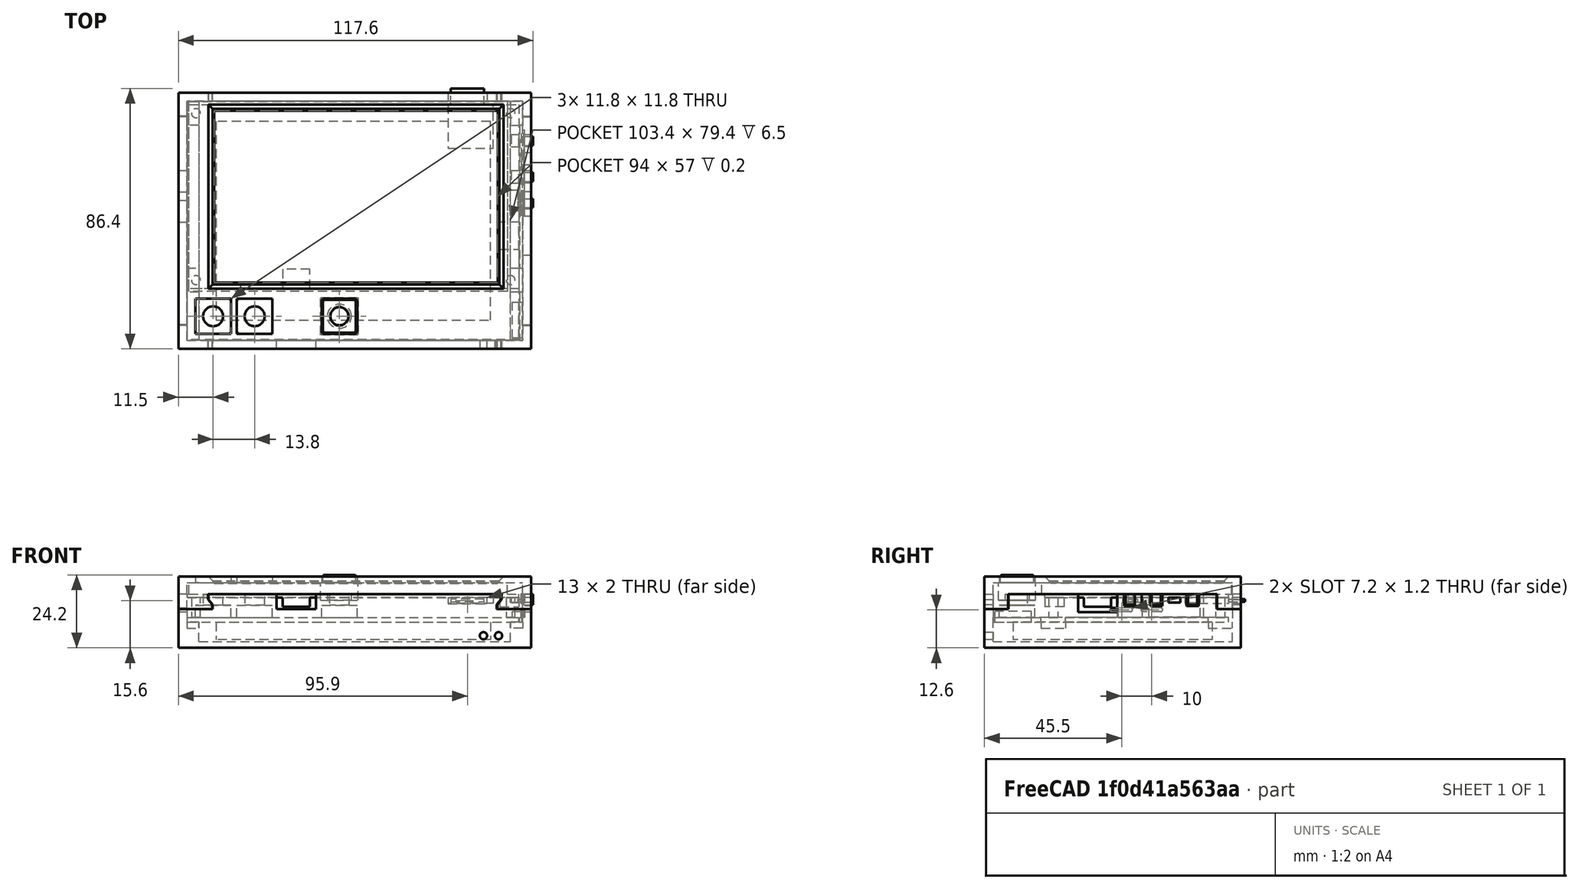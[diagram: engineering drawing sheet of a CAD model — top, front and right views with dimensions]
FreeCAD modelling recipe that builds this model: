
FCSTD DOCUMENT  (FreeCAD 0.19R24276 (Git))
Label: Case-M2
License: All rights reserved
LicenseURL: http://en.wikipedia.org/wiki/All_rights_reserved
objects: Sketcher::SketchObject×50, PartDesign::Pad×27, PartDesign::Pocket×20, PartDesign::ShapeBinder×11, PartDesign::Body×8, Mesh::Feature×3, PartDesign::Chamfer×2, PartDesign::Fillet×1
note: 169 computed .brp shape members not serialized (recipe doc carries the construction recipe); baked Part::Feature solids carry a one-line shape summary decoded from their .brp

FEATURE [Sketcher::SketchObject] Sketch  label="PCB-OUTLINE"
  FullyConstrained = true
  MapMode = 5
  Support = -> [XY_Plane]
  sketch-geometry (41):
    g0: LineSegment StartX=-55 StartY=30.5 StartZ=0 EndX=55 EndY=30.5 EndZ=0
    g1: LineSegment StartX=55 StartY=30.5 StartZ=0 EndX=55 EndY=-30.5 EndZ=0
    g2: LineSegment StartX=55 StartY=-30.5 StartZ=0 EndX=-55 EndY=-30.5 EndZ=0
    g3: LineSegment StartX=-55 StartY=-30.5 StartZ=0 EndX=-55 EndY=30.5 EndZ=0
    g4: Circle CenterX=-52.2 CenterY=27.7 CenterZ=0 NormalX=0 NormalY=0 NormalZ=1 AngleXU=0 Radius=1.6
    g5: Circle CenterX=52.2 CenterY=27.7 CenterZ=0 NormalX=0 NormalY=0 NormalZ=1 AngleXU=0 Radius=1.6
    g6: Circle CenterX=-52.2 CenterY=-27.7 CenterZ=0 NormalX=0 NormalY=0 NormalZ=1 AngleXU=0 Radius=1.6
    g7: Circle CenterX=52.2 CenterY=-27.7 CenterZ=0 NormalX=0 NormalY=0 NormalZ=1 AngleXU=0 Radius=1.6
    g8: LineSegment StartX=31.4 StartY=30.5 StartZ=0 EndX=46.4 EndY=30.5 EndZ=0
    g9: LineSegment StartX=46.4 StartY=30.5 StartZ=0 EndX=46.4 EndY=16 EndZ=0
    g10: LineSegment StartX=46.4 StartY=16 StartZ=0 EndX=31.4 EndY=16 EndZ=0
    g11: LineSegment StartX=31.4 StartY=16 StartZ=0 EndX=31.4 EndY=30.5 EndZ=0
    g12: LineSegment StartX=-23.4 StartY=-24.1 StartZ=0 EndX=-14.4 EndY=-24.1 EndZ=0
    g13: LineSegment StartX=-14.4 StartY=-24.1 StartZ=0 EndX=-14.4 EndY=-30.5 EndZ=0
    g14: LineSegment StartX=-14.4 StartY=-30.5 StartZ=0 EndX=-23.4 EndY=-30.5 EndZ=0
    g15: LineSegment StartX=-23.4 StartY=-30.5 StartZ=0 EndX=-23.4 EndY=-24.1 EndZ=0
    g16: LineSegment StartX=48.6 StartY=-8.5 StartZ=0 EndX=55 EndY=-8.5 EndZ=0
    g17: LineSegment StartX=55 StartY=-8.5 StartZ=0 EndX=55 EndY=-17.5 EndZ=0
    g18: LineSegment StartX=55 StartY=-17.5 StartZ=0 EndX=48.6 EndY=-17.5 EndZ=0
    g19: LineSegment StartX=48.6 StartY=-17.5 StartZ=0 EndX=48.6 EndY=-8.5 EndZ=0
    g20: LineSegment StartX=52 StartY=2.1 StartZ=0 EndX=54.7 EndY=2.1 EndZ=0
    g21: LineSegment StartX=54.7 StartY=2.1 StartZ=0 EndX=54.7 EndY=-4.7 EndZ=0
    g22: LineSegment StartX=54.7 StartY=-4.7 StartZ=0 EndX=52 EndY=-4.7 EndZ=0
    g23: LineSegment StartX=52 StartY=-4.7 StartZ=0 EndX=52 EndY=2.1 EndZ=0
    g24: LineSegment StartX=52.4 StartY=8.5 StartZ=0 EndX=55 EndY=8.5 EndZ=0
    g25: LineSegment StartX=55 StartY=8.5 StartZ=0 EndX=55 EndY=4.5 EndZ=0
    g26: LineSegment StartX=55 StartY=4.5 StartZ=0 EndX=52.4 EndY=4.5 EndZ=0
    g27: LineSegment StartX=52.4 StartY=4.5 StartZ=0 EndX=52.4 EndY=8.5 EndZ=0
    g28: LineSegment StartX=52.4 StartY=20.5 StartZ=0 EndX=55 EndY=20.5 EndZ=0
    g29: LineSegment StartX=55 StartY=20.5 StartZ=0 EndX=55 EndY=16.5 EndZ=0
    g30: LineSegment StartX=55 StartY=16.5 StartZ=0 EndX=52.4 EndY=16.5 EndZ=0
    g31: LineSegment StartX=52.4 StartY=16.5 StartZ=0 EndX=52.4 EndY=20.5 EndZ=0
    g32: LineSegment StartX=32.4 StartY=30.5 StartZ=0 EndX=43.4 EndY=30.5 EndZ=0
    g33: LineSegment StartX=43.4 StartY=30.5 StartZ=0 EndX=43.4 EndY=20.5 EndZ=0
    g34: LineSegment StartX=43.4 StartY=20.5 StartZ=0 EndX=32.4 EndY=20.5 EndZ=0
    g35: LineSegment StartX=32.4 StartY=20.5 StartZ=0 EndX=32.4 EndY=30.5 EndZ=0
    g36: LineSegment StartX=54.7 StartY=0.2 StartZ=0 EndX=56.2 EndY=0.2 EndZ=0
    g37: LineSegment StartX=56.2 StartY=0.2 StartZ=0 EndX=56.2 EndY=-2.8 EndZ=0
    g38: LineSegment StartX=56.2 StartY=-2.8 StartZ=0 EndX=54.7 EndY=-2.8 EndZ=0
    g39: LineSegment StartX=54.7 StartY=-2.8 StartZ=0 EndX=54.7 EndY=0.2 EndZ=0
    g40: LineSegment StartX=54.7 StartY=-1.5 StartZ=0 EndX=56.2 EndY=-1.5 EndZ=0
  constraints (120):
    c: Coincident(g0,g1)
    c: Coincident(g1,g2)
    c: Coincident(g2,g3)
    c: Coincident(g3,g0)
    c: Horizontal(g0)
    c: Vertical(g1)
    c: DistanceX(g2,g2) = 110
    c: Symmetric(g2,g1,g-2)
    c: DistanceY(g3,g3) = 61
    c: Symmetric(g0,g2,g-1)
    c: Symmetric(g6,g7,g-2)
    c: DistanceX(g6,g7) = 104.4
    c: Vertical(g5,g7)
    c: Symmetric(g4,g6,g-1)
    c: Horizontal(g4,g5)
    c: DistanceY(g6,g4) = 55.4
    c: Equal(g4,g6)
    c: Equal(g6,g7)
    c: Equal(g7,g5)
    c: Radius(g4) = 1.6
    c: Coincident(g8,g9)
    c: Coincident(g9,g10)
    c: Coincident(g10,g11)
    c: Coincident(g11,g8)
    c: Horizontal(g8)
    c: Horizontal(g10)
    c: Vertical(g9)
    c: Vertical(g11)
    c: Coincident(g12,g13)
    c: Coincident(g13,g14)
    c: Coincident(g14,g15)
    c: Coincident(g15,g12)
    c: Horizontal(g12)
    c: Horizontal(g14)
    c: Vertical(g13)
    c: Vertical(g15)
    c: Coincident(g16,g17)
    c: Coincident(g17,g18)
    c: Coincident(g18,g19)
    c: Coincident(g19,g16)
    c: Horizontal(g16)
    c: Horizontal(g18)
    c: Vertical(g17)
    c: Vertical(g19)
    c: Coincident(g20,g21)
    c: Coincident(g21,g22)
    c: Coincident(g22,g23)
    c: Coincident(g23,g20)
    c: Horizontal(g20)
    c: Horizontal(g22)
    c: Vertical(g21)
    c: Vertical(g23)
    c: Coincident(g24,g25)
    c: Coincident(g25,g26)
    c: Coincident(g26,g27)
    c: Coincident(g27,g24)
    c: Horizontal(g24)
    c: Horizontal(g26)
    c: Vertical(g25)
    c: Vertical(g27)
    c: Coincident(g28,g29)
    c: Coincident(g29,g30)
    c: Coincident(g30,g31)
    c: Coincident(g31,g28)
    c: Horizontal(g28)
    c: Horizontal(g30)
    c: Vertical(g29)
    c: Vertical(g31)
    c: Equal(g14,g17)
    c: Equal(g18,g13)
    c: DistanceY(g15,g15) = 6.4
    c: DistanceX(g12,g12) = 9
    c: DistanceX(g2,g14) = 31.6
    c: PointOnObject(g14,g2)
    c: PointOnObject(g17,g1)
    c: DistanceY(g1,g17) = 13
    c: DistanceX(g8,g8) = 15
    c: DistanceY(g11,g11) = 14.5
    c: PointOnObject(g8,g0)
    c: Coincident(g32,g33)
    c: Coincident(g33,g34)
    c: Coincident(g34,g35)
    c: Coincident(g35,g32)
    c: Horizontal(g32)
    c: Horizontal(g34)
    c: Vertical(g33)
    c: Vertical(g35)
    c: PointOnObject(g32,g0)
    c: DistanceX(g32,g32) = 11
    c: DistanceX(g8,g32) = 1
    c: DistanceY(g35,g35) = 10
    c: DistanceX(g8,g0) = 8.6
    c: DistanceY(g23,g23) = 6.8
    c: DistanceX(g22,g1) = 3
    c: DistanceX(g22,g22) = 2.7
    c: DistanceY(g20,g0) = 28.4
    c: Equal(g24,g30)
    c: Equal(g27,g31)
    c: PointOnObject(g28,g1)
    c: PointOnObject(g24,g1)
    c: DistanceY(g27,g27) = 4
    c: DistanceX(g26,g26) = 2.6
    c: DistanceY(g24,g0) = 22
    c: DistanceY(g28,g0) = 10
    c: Coincident(g36,g37)
    c: Coincident(g37,g38)
    c: Coincident(g38,g39)
    c: Coincident(g39,g36)
    c: Horizontal(g36)
    c: Horizontal(g38)
    c: Vertical(g37)
    c: Vertical(g39)
    c: PointOnObject(g36,g21)
    c: DistanceY(g37,g37) = 3
    c: DistanceX(g38,g38) = 1.5
    c: DistanceY(g21,g37) = 1.9
    c: PointOnObject(g40,g21)
    c: PointOnObject(g40,g37)
    c: Horizontal(g40)
    c: DistanceY(g37,g40) = 1.3
FEATURE [PartDesign::ShapeBinder] ShapeBinder
  Support = -> [Sketch]
  TraceSupport = false
FEATURE [PartDesign::ShapeBinder] ShapeBinder001
  Support = -> [Sketch]
  TraceSupport = false
FEATURE [Sketcher::SketchObject] Sketch001
  ExternalGeometry = -> [ShapeBinder]
  FullyConstrained = true
  MapMode = 5
  Support = -> [XY_Plane001]
  sketch-geometry (4):
    g0: LineSegment StartX=-55 StartY=30.5 StartZ=0 EndX=55 EndY=30.5 EndZ=0
    g1: LineSegment StartX=55 StartY=30.5 StartZ=0 EndX=55 EndY=-47.5 EndZ=0
    g2: LineSegment StartX=55 StartY=-47.5 StartZ=0 EndX=-55 EndY=-47.5 EndZ=0
    g3: LineSegment StartX=-55 StartY=-47.5 StartZ=0 EndX=-55 EndY=30.5 EndZ=0
  constraints (11):
    c: Coincident(g0,g1)
    c: Coincident(g1,g2)
    c: Coincident(g2,g3)
    c: Coincident(g3,g0)
    c: Horizontal(g0)
    c: Horizontal(g2)
    c: Vertical(g1)
    c: Vertical(g3)
    c: Coincident(g0,g-3)
    c: Vertical(g-4,g1)
    c: DistanceY(g1,g-4) = 17
FEATURE [PartDesign::Pad] Pad
  Direction = (1,1,1)
  Length = 1.6
  Length2 = 100
  Profile = -> Sketch001
  Type = 0
FEATURE [Sketcher::SketchObject] Sketch008  label="LCD_OUTLINE"
  ExternalGeometry = -> [Sketch]
  FullyConstrained = true
  MapMode = 5
  Support = -> [XY_Plane]
  sketch-geometry (8):
    g0: LineSegment StartX=-54.5 StartY=31.5 StartZ=0 EndX=51.1 EndY=31.5 EndZ=0
    g1: LineSegment StartX=51.1 StartY=31.5 StartZ=0 EndX=51.1 EndY=-31.5 EndZ=0
    g2: LineSegment StartX=51.1 StartY=-31.5 StartZ=0 EndX=-54.5 EndY=-31.5 EndZ=0
    g3: LineSegment StartX=-54.5 StartY=-31.5 StartZ=0 EndX=-54.5 EndY=31.5 EndZ=0
    g4: LineSegment StartX=-46.1 StartY=28.5 StartZ=0 EndX=47.9 EndY=28.5 EndZ=0
    g5: LineSegment StartX=47.9 StartY=28.5 StartZ=0 EndX=47.9 EndY=-28.5 EndZ=0
    g6: LineSegment StartX=47.9 StartY=-28.5 StartZ=0 EndX=-46.1 EndY=-28.5 EndZ=0
    g7: LineSegment StartX=-46.1 StartY=-28.5 StartZ=0 EndX=-46.1 EndY=28.5 EndZ=0
  constraints (23):
    c: Coincident(g0,g1)
    c: Coincident(g1,g2)
    c: Coincident(g2,g3)
    c: Coincident(g3,g0)
    c: Horizontal(g0)
    c: Horizontal(g2)
    c: Vertical(g3)
    c: DistanceY(g1,g1) = 63
    c: Symmetric(g1,g0,g-1)
    c: DistanceX(g0,g0) = 105.6
    c: DistanceX(g-3,g0) = 0.5
    c: Coincident(g4,g5)
    c: Coincident(g5,g6)
    c: Coincident(g6,g7)
    c: Coincident(g7,g4)
    c: Horizontal(g4)
    c: Horizontal(g6)
    c: Vertical(g5)
    c: Vertical(g7)
    c: DistanceX(g5,g1) = 3.2
    c: DistanceX(g2,g6) = 8.4
    c: DistanceY(g4,g0) = 3
    c: DistanceY(g1,g5) = 3
FEATURE [PartDesign::ShapeBinder] ShapeBinder002
  Support = -> [Sketch]
  TraceSupport = false
FEATURE [PartDesign::ShapeBinder] ShapeBinder003
  Support = -> [Sketch008]
  TraceSupport = false
FEATURE [Sketcher::SketchObject] Sketch009
  ExternalGeometry = -> [ShapeBinder002]
  FullyConstrained = true
  MapMode = 5
  Placement = pos=(0,0,1.6) rot=(0,0,1;0rad)
  Support = -> [Pad]
  sketch-geometry (4):
    g0: Circle CenterX=-52.2 CenterY=27.7 CenterZ=0 NormalX=0 NormalY=0 NormalZ=1 AngleXU=0 Radius=1.5
    g1: Circle CenterX=-52.2 CenterY=-27.7 CenterZ=0 NormalX=0 NormalY=0 NormalZ=1 AngleXU=0 Radius=1.5
    g2: Circle CenterX=52.2 CenterY=-27.7 CenterZ=0 NormalX=0 NormalY=0 NormalZ=1 AngleXU=0 Radius=1.5
    g3: Circle CenterX=52.2 CenterY=27.7 CenterZ=0 NormalX=0 NormalY=0 NormalZ=1 AngleXU=0 Radius=1.5
  constraints (8):
    c: Coincident(g0,g-3)
    c: Coincident(g1,g-4)
    c: Coincident(g2,g-5)
    c: Coincident(g3,g-6)
    c: Equal(g0,g1)
    c: Equal(g1,g2)
    c: Equal(g2,g3)
    c: Radius(g0) = 1.5
FEATURE [PartDesign::Pad] Pad001
  BaseFeature = -> Pad
  Direction = (1,1,1)
  Length = 6.5
  Length2 = 100
  Profile = -> Sketch009
  Type = 0
FEATURE [Sketcher::SketchObject] Sketch010
  ExternalGeometry = -> [ShapeBinder002]
  FullyConstrained = true
  MapMode = 5
  Placement = pos=(0,0,8.1) rot=(0,0,1;0rad)
  Support = -> [Pad001]
  sketch-geometry (4):
    g0: LineSegment StartX=-55 StartY=30.5 StartZ=0 EndX=55 EndY=30.5 EndZ=0
    g1: LineSegment StartX=55 StartY=30.5 StartZ=0 EndX=55 EndY=-30.5 EndZ=0
    g2: LineSegment StartX=55 StartY=-30.5 StartZ=0 EndX=-55 EndY=-30.5 EndZ=0
    g3: LineSegment StartX=-55 StartY=-30.5 StartZ=0 EndX=-55 EndY=30.5 EndZ=0
  constraints (10):
    c: Coincident(g0,g1)
    c: Coincident(g1,g2)
    c: Coincident(g2,g3)
    c: Coincident(g3,g0)
    c: Horizontal(g0)
    c: Horizontal(g2)
    c: Vertical(g1)
    c: Vertical(g3)
    c: Coincident(g0,g-3)
    c: Coincident(g1,g-4)
FEATURE [PartDesign::Pad] Pad002
  BaseFeature = -> Pad001
  Direction = (1,1,1)
  Length = 1.2
  Length2 = 100
  Profile = -> Sketch010
  Type = 0
FEATURE [Sketcher::SketchObject] Sketch011
  ExternalGeometry = -> [ShapeBinder003]
  FullyConstrained = true
  MapMode = 5
  Placement = pos=(0,0,9.3) rot=(0,0,1;0rad)
  Support = -> [Pad002]
  sketch-geometry (4):
    g0: LineSegment StartX=-54.5 StartY=31.5 StartZ=0 EndX=51.1 EndY=31.5 EndZ=0
    g1: LineSegment StartX=51.1 StartY=31.5 StartZ=0 EndX=51.1 EndY=-31.5 EndZ=0
    g2: LineSegment StartX=51.1 StartY=-31.5 StartZ=0 EndX=-54.5 EndY=-31.5 EndZ=0
    g3: LineSegment StartX=-54.5 StartY=-31.5 StartZ=0 EndX=-54.5 EndY=31.5 EndZ=0
  constraints (10):
    c: Coincident(g0,g1)
    c: Coincident(g1,g2)
    c: Coincident(g2,g3)
    c: Coincident(g3,g0)
    c: Horizontal(g0)
    c: Horizontal(g2)
    c: Vertical(g1)
    c: Vertical(g3)
    c: Coincident(g0,g-3)
    c: Coincident(g1,g-4)
FEATURE [PartDesign::Pad] Pad003
  BaseFeature = -> Pad002
  Direction = (1,1,1)
  Length = 3.8
  Length2 = 100
  Profile = -> Sketch011
  Type = 0
FEATURE [Sketcher::SketchObject] Sketch012
  ExternalGeometry = -> [ShapeBinder003]
  FullyConstrained = true
  MapMode = 5
  Placement = pos=(0,0,13.1) rot=(0,0,1;0rad)
  Support = -> [Pad003]
  sketch-geometry (4):
    g0: LineSegment StartX=-46.1 StartY=28.5 StartZ=0 EndX=47.9 EndY=28.5 EndZ=0
    g1: LineSegment StartX=47.9 StartY=28.5 StartZ=0 EndX=47.9 EndY=-28.5 EndZ=0
    g2: LineSegment StartX=47.9 StartY=-28.5 StartZ=0 EndX=-46.1 EndY=-28.5 EndZ=0
    g3: LineSegment StartX=-46.1 StartY=-28.5 StartZ=0 EndX=-46.1 EndY=28.5 EndZ=0
  constraints (10):
    c: Coincident(g0,g1)
    c: Coincident(g1,g2)
    c: Coincident(g2,g3)
    c: Coincident(g3,g0)
    c: Horizontal(g0)
    c: Horizontal(g2)
    c: Vertical(g1)
    c: Vertical(g3)
    c: Coincident(g0,g-3)
    c: Coincident(g1,g-4)
FEATURE [PartDesign::Pocket] Pocket
  BaseFeature = -> Pad003
  Length = 0.2
  Length2 = 100
  Profile = -> Sketch012
  Type = 0
FEATURE [Sketcher::SketchObject] Sketch013
  ExternalGeometry = -> [ShapeBinder002]
  FullyConstrained = true
  MapMode = 5
  Placement = pos=(0,0,8.1) rot=(1,0,0;3.14159rad)
  Support = -> [Pocket]
  sketch-geometry (8):
    g0: LineSegment StartX=-23.4 StartY=30.5 StartZ=0 EndX=-14.4 EndY=30.5 EndZ=0
    g1: LineSegment StartX=-14.4 StartY=30.5 StartZ=0 EndX=-14.4 EndY=24.1 EndZ=0
    g2: LineSegment StartX=-14.4 StartY=24.1 StartZ=0 EndX=-23.4 EndY=24.1 EndZ=0
    g3: LineSegment StartX=-23.4 StartY=24.1 StartZ=0 EndX=-23.4 EndY=30.5 EndZ=0
    g4: LineSegment StartX=48.6 StartY=17.5 StartZ=0 EndX=55 EndY=17.5 EndZ=0
    g5: LineSegment StartX=55 StartY=17.5 StartZ=0 EndX=55 EndY=8.5 EndZ=0
    g6: LineSegment StartX=55 StartY=8.5 StartZ=0 EndX=48.6 EndY=8.5 EndZ=0
    g7: LineSegment StartX=48.6 StartY=8.5 StartZ=0 EndX=48.6 EndY=17.5 EndZ=0
  constraints (20):
    c: Coincident(g0,g1)
    c: Coincident(g1,g2)
    c: Coincident(g2,g3)
    c: Coincident(g3,g0)
    c: Horizontal(g0)
    c: Horizontal(g2)
    c: Vertical(g1)
    c: Vertical(g3)
    c: Coincident(g0,g-3)
    c: Coincident(g1,g-4)
    c: Coincident(g4,g5)
    c: Coincident(g5,g6)
    c: Coincident(g6,g7)
    c: Coincident(g7,g4)
    c: Horizontal(g4)
    c: Horizontal(g6)
    c: Vertical(g5)
    c: Vertical(g7)
    c: Coincident(g4,g-6)
    c: Coincident(g5,g-5)
FEATURE [PartDesign::Pad] Pad004
  BaseFeature = -> Pocket
  Direction = (1,1,1)
  Length = 3
  Length2 = 100
  Profile = -> Sketch013
  Type = 0
FEATURE [Sketcher::SketchObject] Sketch014
  ExternalGeometry = -> [ShapeBinder002]
  FullyConstrained = true
  MapMode = 5
  Placement = pos=(0,0,8.1) rot=(1,0,0;3.14159rad)
  Support = -> [Pad004]
  sketch-geometry (4):
    g0: LineSegment StartX=31.4 StartY=-16 StartZ=0 EndX=46.4 EndY=-16 EndZ=0
    g1: LineSegment StartX=46.4 StartY=-16 StartZ=0 EndX=46.4 EndY=-30.5 EndZ=0
    g2: LineSegment StartX=46.4 StartY=-30.5 StartZ=0 EndX=31.4 EndY=-30.5 EndZ=0
    g3: LineSegment StartX=31.4 StartY=-30.5 StartZ=0 EndX=31.4 EndY=-16 EndZ=0
  constraints (10):
    c: Coincident(g0,g1)
    c: Coincident(g1,g2)
    c: Coincident(g2,g3)
    c: Coincident(g3,g0)
    c: Horizontal(g0)
    c: Horizontal(g2)
    c: Vertical(g1)
    c: Vertical(g3)
    c: Coincident(g0,g-3)
    c: Coincident(g1,g-4)
FEATURE [PartDesign::Pad] Pad005
  BaseFeature = -> Pad004
  Direction = (1,1,1)
  Length = 1.8
  Length2 = 100
  Profile = -> Sketch014
  Type = 0
FEATURE [Sketcher::SketchObject] Sketch015
  ExternalGeometry = -> [Pad005,ShapeBinder002]
  FullyConstrained = true
  MapMode = 5
  Placement = pos=(0,30.5,0) rot=(0,0.707107,0.707107;3.14159rad)
  Support = -> [Pad005]
  sketch-geometry (4):
    g0: LineSegment StartX=-43.4 StartY=7.6 StartZ=0 EndX=-32.4 EndY=7.6 EndZ=0
    g1: LineSegment StartX=-32.4 StartY=7.6 StartZ=0 EndX=-32.4 EndY=6.7 EndZ=0
    g2: LineSegment StartX=-32.4 StartY=6.7 StartZ=0 EndX=-43.4 EndY=6.7 EndZ=0
    g3: LineSegment StartX=-43.4 StartY=6.7 StartZ=0 EndX=-43.4 EndY=7.6 EndZ=0
  constraints (12):
    c: Coincident(g0,g1)
    c: Coincident(g1,g2)
    c: Coincident(g2,g3)
    c: Coincident(g3,g0)
    c: Horizontal(g0)
    c: Horizontal(g2)
    c: Vertical(g1)
    c: Vertical(g3)
    c: DistanceY(g1,g1) = 0.9
    c: Vertical(g2,g-5)
    c: Vertical(g1,g-6)
    c: DistanceY(g-4,g1) = 0.4
FEATURE [PartDesign::Pad] Pad006
  BaseFeature = -> Pad005
  Direction = (1,1,1)
  Length = 5.4
  Length2 = 100
  Profile = -> Sketch015
  Type = 0
FEATURE [Sketcher::SketchObject] Sketch016
  ExternalGeometry = -> [ShapeBinder002]
  FullyConstrained = true
  MapMode = 5
  Placement = pos=(0,0,8.1) rot=(1,0,0;3.14159rad)
  Support = -> [Pad006]
  sketch-geometry (12):
    g0: LineSegment StartX=52 StartY=4.7 StartZ=0 EndX=54.7 EndY=4.7 EndZ=0
    g1: LineSegment StartX=54.7 StartY=4.7 StartZ=0 EndX=54.7 EndY=-2.1 EndZ=0
    g2: LineSegment StartX=54.7 StartY=-2.1 StartZ=0 EndX=52 EndY=-2.1 EndZ=0
    g3: LineSegment StartX=52 StartY=-2.1 StartZ=0 EndX=52 EndY=4.7 EndZ=0
    g4: LineSegment StartX=52.4 StartY=-4.5 StartZ=0 EndX=55 EndY=-4.5 EndZ=0
    g5: LineSegment StartX=55 StartY=-4.5 StartZ=0 EndX=55 EndY=-8.5 EndZ=0
    g6: LineSegment StartX=55 StartY=-8.5 StartZ=0 EndX=52.4 EndY=-8.5 EndZ=0
    g7: LineSegment StartX=52.4 StartY=-8.5 StartZ=0 EndX=52.4 EndY=-4.5 EndZ=0
    g8: LineSegment StartX=52.4 StartY=-16.5 StartZ=0 EndX=55 EndY=-16.5 EndZ=0
    g9: LineSegment StartX=55 StartY=-16.5 StartZ=0 EndX=55 EndY=-20.5 EndZ=0
    g10: LineSegment StartX=55 StartY=-20.5 StartZ=0 EndX=52.4 EndY=-20.5 EndZ=0
    g11: LineSegment StartX=52.4 StartY=-20.5 StartZ=0 EndX=52.4 EndY=-16.5 EndZ=0
  constraints (30):
    c: Coincident(g0,g1)
    c: Coincident(g1,g2)
    c: Coincident(g2,g3)
    c: Coincident(g3,g0)
    c: Horizontal(g0)
    c: Horizontal(g2)
    c: Vertical(g1)
    c: Vertical(g3)
    c: Coincident(g0,g-3)
    c: Coincident(g1,g-4)
    c: Coincident(g4,g5)
    c: Coincident(g5,g6)
    c: Coincident(g6,g7)
    c: Coincident(g7,g4)
    c: Horizontal(g4)
    c: Horizontal(g6)
    c: Vertical(g5)
    c: Vertical(g7)
    c: Coincident(g4,g-5)
    c: Coincident(g5,g-6)
    c: Coincident(g8,g9)
    c: Coincident(g9,g10)
    c: Coincident(g10,g11)
    c: Coincident(g11,g8)
    c: Horizontal(g8)
    c: Horizontal(g10)
    c: Vertical(g9)
    c: Vertical(g11)
    c: Coincident(g8,g-7)
    c: Coincident(g9,g-8)
FEATURE [PartDesign::Pad] Pad007
  BaseFeature = -> Pad006
  Direction = (1,1,1)
  Length = 1.6
  Length2 = 100
  Profile = -> Sketch016
  Type = 0
FEATURE [Sketcher::SketchObject] Sketch017
  ExternalGeometry = -> [ShapeBinder002,Pad007]
  FullyConstrained = true
  MapMode = 5
  Placement = pos=(54.7,0,0) rot=(0.57735,0.57735,0.57735;2.0944rad)
  Support = -> [Pad007]
  sketch-geometry (8):
    g0: LineSegment StartX=-2.8 StartY=7.7 StartZ=0 EndX=-1.5 EndY=7.7 EndZ=0
    g1: LineSegment StartX=-1.5 StartY=7.7 StartZ=0 EndX=-1.5 EndY=6.7 EndZ=0
    g2: LineSegment StartX=-1.5 StartY=6.7 StartZ=0 EndX=-2.8 EndY=6.7 EndZ=0
    g3: LineSegment StartX=-2.8 StartY=6.7 StartZ=0 EndX=-2.8 EndY=7.7 EndZ=0
    g4: LineSegment StartX=-1.1 StartY=7.7 StartZ=0 EndX=0.2 EndY=7.7 EndZ=0
    g5: LineSegment StartX=0.2 StartY=7.7 StartZ=0 EndX=0.2 EndY=6.7 EndZ=0
    g6: LineSegment StartX=0.2 StartY=6.7 StartZ=0 EndX=-1.1 EndY=6.7 EndZ=0
    g7: LineSegment StartX=-1.1 StartY=6.7 StartZ=0 EndX=-1.1 EndY=7.7 EndZ=0
  constraints (24):
    c: Coincident(g0,g1)
    c: Coincident(g1,g2)
    c: Coincident(g2,g3)
    c: Coincident(g3,g0)
    c: Horizontal(g0)
    c: Horizontal(g2)
    c: Vertical(g1)
    c: Vertical(g3)
    c: Coincident(g4,g5)
    c: Coincident(g5,g6)
    c: Coincident(g6,g7)
    c: Coincident(g7,g4)
    c: Horizontal(g4)
    c: Horizontal(g6)
    c: Vertical(g5)
    c: Vertical(g7)
    c: Vertical(g-3,g2)
    c: Vertical(g-4,g1)
    c: Vertical(g5,g-5)
    c: Horizontal(g0,g4)
    c: Equal(g1,g7)
    c: DistanceY(g5,g5) = 1
    c: DistanceY(g-6,g2) = 0.2
    c: DistanceX(g4,g4) = 1.3
FEATURE [PartDesign::Pad] Pad008
  BaseFeature = -> Pad007
  Direction = (1,1,1)
  Length = 1.5
  Length2 = 100
  Profile = -> Sketch017
  Type = 0
FEATURE [Sketcher::SketchObject] Sketch018
  ExternalGeometry = -> [Pad008]
  FullyConstrained = true
  MapMode = 5
  Placement = pos=(0,0,1.6) rot=(0,0,1;0rad)
  Support = -> [Pad008]
  sketch-geometry (12):
    g0: LineSegment StartX=-10.5 StartY=-33.8 StartZ=0 EndX=1.3 EndY=-33.8 EndZ=0
    g1: LineSegment StartX=1.3 StartY=-33.8 StartZ=0 EndX=1.3 EndY=-45.6 EndZ=0
    g2: LineSegment StartX=1.3 StartY=-45.6 StartZ=0 EndX=-10.5 EndY=-45.6 EndZ=0
    g3: LineSegment StartX=-10.5 StartY=-45.6 StartZ=0 EndX=-10.5 EndY=-33.8 EndZ=0
    g4: LineSegment StartX=-38.6 StartY=-33.8 StartZ=0 EndX=-26.8 EndY=-33.8 EndZ=0
    g5: LineSegment StartX=-26.8 StartY=-33.8 StartZ=0 EndX=-26.8 EndY=-45.6 EndZ=0
    g6: LineSegment StartX=-26.8 StartY=-45.6 StartZ=0 EndX=-38.6 EndY=-45.6 EndZ=0
    g7: LineSegment StartX=-38.6 StartY=-45.6 StartZ=0 EndX=-38.6 EndY=-33.8 EndZ=0
    g8: LineSegment StartX=-52.4 StartY=-33.8 StartZ=0 EndX=-40.6 EndY=-33.8 EndZ=0
    g9: LineSegment StartX=-40.6 StartY=-33.8 StartZ=0 EndX=-40.6 EndY=-45.6 EndZ=0
    g10: LineSegment StartX=-40.6 StartY=-45.6 StartZ=0 EndX=-52.4 EndY=-45.6 EndZ=0
    g11: LineSegment StartX=-52.4 StartY=-45.6 StartZ=0 EndX=-52.4 EndY=-33.8 EndZ=0
  constraints (36):
    c: Coincident(g0,g1)
    c: Coincident(g1,g2)
    c: Coincident(g2,g3)
    c: Coincident(g3,g0)
    c: Horizontal(g0)
    c: Horizontal(g2)
    c: Vertical(g1)
    c: Vertical(g3)
    c: Coincident(g4,g5)
    c: Coincident(g5,g6)
    c: Coincident(g6,g7)
    c: Coincident(g7,g4)
    c: Horizontal(g4)
    c: Horizontal(g6)
    c: Vertical(g5)
    c: Vertical(g7)
    c: Coincident(g8,g9)
    c: Coincident(g9,g10)
    c: Coincident(g10,g11)
    c: Coincident(g11,g8)
    c: Horizontal(g8)
    c: Horizontal(g10)
    c: Vertical(g9)
    c: Vertical(g11)
    c: Equal(g8,g4)
    c: Equal(g4,g0)
    c: Equal(g9,g5)
    c: Equal(g5,g1)
    c: DistanceY(g11,g11) = 11.8
    c: Horizontal(g8,g4)
    c: Horizontal(g4,g0)
    c: DistanceY(g-4,g10) = 1.9
    c: DistanceX(g-4,g10) = 2.6
    c: DistanceX(g-4,g6) = 16.4
    c: DistanceX(g-4,g2) = 44.5
    c: Equal(g0,g1)
FEATURE [PartDesign::Pad] Pad009
  BaseFeature = -> Pad008
  Direction = (1,1,1)
  Length = 4
  Length2 = 100
  Profile = -> Sketch018
  Type = 0
FEATURE [Sketcher::SketchObject] Sketch019
  ExternalGeometry = -> [Pad009]
  FullyConstrained = true
  MapMode = 5
  Placement = pos=(0,0,5.6) rot=(0,0,1;0rad)
  Support = -> [Pad009]
  sketch-geometry (3):
    g0: Circle CenterX=-46.5 CenterY=-39.7 CenterZ=0 NormalX=0 NormalY=0 NormalZ=1 AngleXU=0 Radius=3.3
    g1: Circle CenterX=-32.7 CenterY=-39.7 CenterZ=0 NormalX=0 NormalY=0 NormalZ=1 AngleXU=0 Radius=3.3
    g2: Circle CenterX=-4.6 CenterY=-39.7 CenterZ=0 NormalX=0 NormalY=0 NormalZ=1 AngleXU=0 Radius=3.3
  constraints (9):
    c: Horizontal(g0,g1)
    c: Horizontal(g1,g2)
    c: Equal(g0,g1)
    c: Equal(g1,g2)
    c: Radius(g2) = 3.3
    c: DistanceX(g-3,g0) = 5.9
    c: DistanceY(g-3,g0) = 5.9
    c: DistanceX(g-4,g1) = 5.9
    c: DistanceX(g-5,g2) = 5.9
FEATURE [PartDesign::Pad] Pad010
  BaseFeature = -> Pad009
  Direction = (1,1,1)
  Length = 3.6
  Length2 = 100
  Profile = -> Sketch019
  Type = 0
FEATURE [Sketcher::SketchObject] Sketch020
  FullyConstrained = true
  MapMode = 5
  Placement = pos=(0,0,0) rot=(1,0,0;3.14159rad)
  Support = -> [Pad010]
  sketch-geometry (4):
    g0: LineSegment StartX=-45.5 StartY=41 StartZ=0 EndX=45.5 EndY=41 EndZ=0
    g1: LineSegment StartX=45.5 StartY=41 StartZ=0 EndX=45.5 EndY=-25 EndZ=0
    g2: LineSegment StartX=45.5 StartY=-25 StartZ=0 EndX=-45.5 EndY=-25 EndZ=0
    g3: LineSegment StartX=-45.5 StartY=-25 StartZ=0 EndX=-45.5 EndY=41 EndZ=0
  constraints (11):
    c: Coincident(g0,g1)
    c: Coincident(g1,g2)
    c: Coincident(g2,g3)
    c: Coincident(g3,g0)
    c: Horizontal(g2)
    c: Vertical(g1)
    c: Vertical(g3)
    c: Symmetric(g0,g0,g-2)
    c: DistanceX(g2,g2) = 91
    c: DistanceY(g3,g3) = 66
    c: DistanceY(g2,g-1) = 25
FEATURE [PartDesign::Pad] Pad011
  BaseFeature = -> Pad010
  Direction = (1,1,1)
  Length = 5.8
  Length2 = 100
  Profile = -> Sketch020
  Type = 0
FEATURE [PartDesign::Body] Body001  label="PCB"
  Group = -> [ShapeBinder,ShapeBinder001,ShapeBinder002,ShapeBinder003,Sketch001,Pad,Sketch009,Pad001,Sketch010,Pad002,Sketch011,Pad003,Sketch012,Pocket,Sketch013,Pad004,Sketch014,Pad005,Sketch015,Pad006,Sketch016,Pad007,Sketch017,Pad008,Sketch018,Pad009,Sketch019,Pad010,Sketch020,Pad011]
  Origin = -> Origin001
  Placement = pos=(0,0,8.5) rot=(0,0,1;0rad)
  Tip = -> Pad011
FEATURE [PartDesign::ShapeBinder] ShapeBinder004
  Support = -> [Sketch]
  TraceSupport = false
FEATURE [PartDesign::ShapeBinder] ShapeBinder005
  Support = -> [Sketch008]
  TraceSupport = false
FEATURE [Sketcher::SketchObject] Sketch021
  ExternalGeometry = -> [ShapeBinder005,ShapeBinder004]
  FullyConstrained = true
  MapMode = 5
  Support = -> [XY_Plane002]
  sketch-geometry (4):
    g0: LineSegment StartX=-58 StartY=34.5 StartZ=0 EndX=59 EndY=34.5 EndZ=0
    g1: LineSegment StartX=59 StartY=34.5 StartZ=0 EndX=59 EndY=-50.5 EndZ=0
    g2: LineSegment StartX=59 StartY=-50.5 StartZ=0 EndX=-58 EndY=-50.5 EndZ=0
    g3: LineSegment StartX=-58 StartY=-50.5 StartZ=0 EndX=-58 EndY=34.5 EndZ=0
  constraints (12):
    c: Coincident(g0,g1)
    c: Coincident(g1,g2)
    c: Coincident(g2,g3)
    c: Coincident(g3,g0)
    c: Horizontal(g0)
    c: Horizontal(g2)
    c: Vertical(g1)
    c: Vertical(g3)
    c: DistanceX(g0,g-5) = 3
    c: DistanceX(g-4,g0) = 4
    c: DistanceY(g-3,g0) = 3
    c: DistanceY(g2,g-5) = 20
FEATURE [PartDesign::Pad] Pad012
  Direction = (1,1,1)
  Length = 17.8
  Length2 = 100
  Profile = -> Sketch021
  Type = 0
FEATURE [PartDesign::ShapeBinder] ShapeBinder006
  Support = -> [Sketch]
  TraceSupport = false
FEATURE [PartDesign::ShapeBinder] ShapeBinder007
  Support = -> [Sketch008]
  TraceSupport = false
FEATURE [Sketcher::SketchObject] Sketch022
  AttachmentOffset = pos=(0,0,23.6) rot=(0,0,1;0rad)
  ExternalGeometry = -> [ShapeBinder007,ShapeBinder006]
  FullyConstrained = true
  MapMode = 5
  Placement = pos=(0,0,23.6) rot=(0,0,1;0rad)
  Support = -> [XY_Plane003]
  sketch-geometry (4):
    g0: LineSegment StartX=-58 StartY=34.5 StartZ=0 EndX=59 EndY=34.5 EndZ=0
    g1: LineSegment StartX=59 StartY=34.5 StartZ=0 EndX=59 EndY=-50.5 EndZ=0
    g2: LineSegment StartX=59 StartY=-50.5 StartZ=0 EndX=-58 EndY=-50.5 EndZ=0
    g3: LineSegment StartX=-58 StartY=-50.5 StartZ=0 EndX=-58 EndY=34.5 EndZ=0
  constraints (12):
    c: Coincident(g0,g1)
    c: Coincident(g1,g2)
    c: Coincident(g2,g3)
    c: Coincident(g3,g0)
    c: Horizontal(g0)
    c: Horizontal(g2)
    c: Vertical(g1)
    c: Vertical(g3)
    c: DistanceX(g-5,g0) = 4
    c: DistanceX(g0,g-4) = 3
    c: DistanceY(g-3,g0) = 3
    c: DistanceY(g2,g-4) = 20
FEATURE [PartDesign::Pad] Pad013
  Direction = (1,1,1)
  Length = 5.8
  Length2 = 100
  Profile = -> Sketch022
  Reversed = true
  Type = 0
FEATURE [Sketcher::SketchObject] Sketch023
  ExternalGeometry = -> [ShapeBinder007]
  FullyConstrained = true
  MapMode = 5
  Placement = pos=(0,0,23.6) rot=(0,0,1;0rad)
  Support = -> [Pad013]
  sketch-geometry (4):
    g0: LineSegment StartX=-46.7 StartY=29.1 StartZ=0 EndX=48.5 EndY=29.1 EndZ=0
    g1: LineSegment StartX=48.5 StartY=29.1 StartZ=0 EndX=48.5 EndY=-29.1 EndZ=0
    g2: LineSegment StartX=48.5 StartY=-29.1 StartZ=0 EndX=-46.7 EndY=-29.1 EndZ=0
    g3: LineSegment StartX=-46.7 StartY=-29.1 StartZ=0 EndX=-46.7 EndY=29.1 EndZ=0
  constraints (12):
    c: Coincident(g0,g1)
    c: Coincident(g1,g2)
    c: Coincident(g2,g3)
    c: Coincident(g3,g0)
    c: Horizontal(g0)
    c: Horizontal(g2)
    c: Vertical(g1)
    c: Vertical(g3)
    c: DistanceX(g-3,g0) = 0.6
    c: DistanceY(g-3,g0) = 0.6
    c: DistanceX(g2,g-4) = 0.6
    c: DistanceY(g2,g-4) = 0.6
FEATURE [PartDesign::Pocket] Pocket001
  BaseFeature = -> Pad013
  Length = 5
  Length2 = 100
  Profile = -> Sketch023
  Type = 1
FEATURE [Sketcher::SketchObject] Sketch024
  ExternalGeometry = -> [ShapeBinder006,ShapeBinder007]
  FullyConstrained = true
  MapMode = 5
  Placement = pos=(0,0,17.8) rot=(1,0,0;3.14159rad)
  Support = -> [Pocket001]
  sketch-geometry (4):
    g0: LineSegment StartX=-55.2 StartY=47.7 StartZ=0 EndX=56.2 EndY=47.7 EndZ=0
    g1: LineSegment StartX=56.2 StartY=47.7 StartZ=0 EndX=56.2 EndY=-31.7 EndZ=0
    g2: LineSegment StartX=56.2 StartY=-31.7 StartZ=0 EndX=-55.2 EndY=-31.7 EndZ=0
    g3: LineSegment StartX=-55.2 StartY=-31.7 StartZ=0 EndX=-55.2 EndY=47.7 EndZ=0
  constraints (12):
    c: Coincident(g0,g1)
    c: Coincident(g1,g2)
    c: Coincident(g2,g3)
    c: Coincident(g3,g0)
    c: Horizontal(g0)
    c: Horizontal(g2)
    c: Vertical(g1)
    c: Vertical(g3)
    c: DistanceY(g2,g-5) = 0.2
    c: DistanceX(g2,g-3) = 0.2
    c: DistanceX(g-4,g1) = 1.2
    c: DistanceY(g-4,g0) = 17.2
FEATURE [PartDesign::Pocket] Pocket002
  BaseFeature = -> Pocket001
  Length = 3.8
  Length2 = 100
  Profile = -> Sketch024
  Type = 0
FEATURE [Sketcher::SketchObject] Sketch025
  ExternalGeometry = -> [ShapeBinder005,ShapeBinder004]
  FullyConstrained = true
  MapMode = 5
  Placement = pos=(0,0,17.8) rot=(0,0,1;0rad)
  Support = -> [Pad012]
  sketch-geometry (4):
    g0: LineSegment StartX=-55.2 StartY=31.7 StartZ=0 EndX=56.2 EndY=31.7 EndZ=0
    g1: LineSegment StartX=56.2 StartY=31.7 StartZ=0 EndX=56.2 EndY=-47.7 EndZ=0
    g2: LineSegment StartX=56.2 StartY=-47.7 StartZ=0 EndX=-55.2 EndY=-47.7 EndZ=0
    g3: LineSegment StartX=-55.2 StartY=-47.7 StartZ=0 EndX=-55.2 EndY=31.7 EndZ=0
  constraints (12):
    c: Coincident(g0,g1)
    c: Coincident(g1,g2)
    c: Coincident(g2,g3)
    c: Coincident(g3,g0)
    c: Horizontal(g0)
    c: Horizontal(g2)
    c: Vertical(g1)
    c: Vertical(g3)
    c: DistanceY(g-3,g0) = 0.2
    c: DistanceX(g0,g-4) = 0.2
    c: DistanceX(g-5,g0) = 1.2
    c: DistanceY(g1,g-5) = 17.2
FEATURE [PartDesign::Pocket] Pocket003
  BaseFeature = -> Pad012
  Length = 15.8
  Length2 = 100
  Profile = -> Sketch025
  Type = 0
FEATURE [Sketcher::SketchObject] Sketch026
  ExternalGeometry = -> [Pocket003]
  FullyConstrained = true
  MapMode = 5
  Placement = pos=(0,0,2) rot=(0,0,1;0rad)
  Support = -> [Pocket003]
  sketch-geometry (8):
    g0: LineSegment StartX=-55.2 StartY=31.7 StartZ=0 EndX=-51.2 EndY=31.7 EndZ=0
    g1: LineSegment StartX=-51.2 StartY=31.7 StartZ=0 EndX=-51.2 EndY=-47.7 EndZ=0
    g2: LineSegment StartX=-51.2 StartY=-47.7 StartZ=0 EndX=-55.2 EndY=-47.7 EndZ=0
    g3: LineSegment StartX=-55.2 StartY=-47.7 StartZ=0 EndX=-55.2 EndY=31.7 EndZ=0
    g4: LineSegment StartX=52.2 StartY=31.7 StartZ=0 EndX=56.2 EndY=31.7 EndZ=0
    g5: LineSegment StartX=56.2 StartY=31.7 StartZ=0 EndX=56.2 EndY=-47.7 EndZ=0
    g6: LineSegment StartX=56.2 StartY=-47.7 StartZ=0 EndX=52.2 EndY=-47.7 EndZ=0
    g7: LineSegment StartX=52.2 StartY=-47.7 StartZ=0 EndX=52.2 EndY=31.7 EndZ=0
  constraints (21):
    c: Coincident(g0,g1)
    c: Coincident(g1,g2)
    c: Coincident(g2,g3)
    c: Coincident(g3,g0)
    c: Horizontal(g0)
    c: Horizontal(g2)
    c: Vertical(g1)
    c: Vertical(g3)
    c: Coincident(g4,g5)
    c: Coincident(g5,g6)
    c: Coincident(g6,g7)
    c: Coincident(g7,g4)
    c: Horizontal(g4)
    c: Horizontal(g6)
    c: Vertical(g7)
    c: Equal(g0,g4)
    c: Equal(g1,g7)
    c: Coincident(g-3,g2)
    c: Coincident(g5,g-4)
    c: Coincident(g4,g-4)
    c: DistanceX(g6,g6) = 4
FEATURE [PartDesign::Pad] Pad014
  BaseFeature = -> Pocket003
  Direction = (1,1,1)
  Length = 6.5
  Length2 = 100
  Profile = -> Sketch026
  Type = 0
FEATURE [PartDesign::ShapeBinder] ShapeBinder008
  Support = -> [Sketch]
  TraceSupport = false
FEATURE [Sketcher::SketchObject] Sketch027
  ExternalGeometry = -> [ShapeBinder008,Pad014]
  FullyConstrained = true
  MapMode = 5
  Placement = pos=(0,0,8.5) rot=(0,0,1;0rad)
  Support = -> [Pad014]
  sketch-geometry (16):
    g0: LineSegment StartX=-55.2 StartY=31.7 StartZ=0 EndX=-51.2 EndY=31.7 EndZ=0
    g1: LineSegment StartX=-51.2 StartY=31.7 StartZ=0 EndX=-51.2 EndY=23.7 EndZ=0
    g2: LineSegment StartX=-51.2 StartY=23.7 StartZ=0 EndX=-55.2 EndY=23.7 EndZ=0
    g3: LineSegment StartX=-55.2 StartY=23.7 StartZ=0 EndX=-55.2 EndY=31.7 EndZ=0
    g4: LineSegment StartX=56.2 StartY=31.7 StartZ=0 EndX=52.2 EndY=31.7 EndZ=0
    g5: LineSegment StartX=52.2 StartY=31.7 StartZ=0 EndX=52.2 EndY=23.7 EndZ=0
    g6: LineSegment StartX=52.2 StartY=23.7 StartZ=0 EndX=56.2 EndY=23.7 EndZ=0
    g7: LineSegment StartX=56.2 StartY=23.7 StartZ=0 EndX=56.2 EndY=31.7 EndZ=0
    g8: LineSegment StartX=-55.2 StartY=-23.7 StartZ=0 EndX=-51.2 EndY=-23.7 EndZ=0
    g9: LineSegment StartX=-51.2 StartY=-23.7 StartZ=0 EndX=-51.2 EndY=-31.7 EndZ=0
    g10: LineSegment StartX=-51.2 StartY=-31.7 StartZ=0 EndX=-55.2 EndY=-31.7 EndZ=0
    g11: LineSegment StartX=-55.2 StartY=-31.7 StartZ=0 EndX=-55.2 EndY=-23.7 EndZ=0
    g12: LineSegment StartX=52.2 StartY=-23.7 StartZ=0 EndX=56.2 EndY=-23.7 EndZ=0
    g13: LineSegment StartX=56.2 StartY=-23.7 StartZ=0 EndX=56.2 EndY=-31.7 EndZ=0
    g14: LineSegment StartX=56.2 StartY=-31.7 StartZ=0 EndX=52.2 EndY=-31.7 EndZ=0
    g15: LineSegment StartX=52.2 StartY=-31.7 StartZ=0 EndX=52.2 EndY=-23.7 EndZ=0
  constraints (46):
    c: Coincident(g0,g1)
    c: Coincident(g1,g2)
    c: Coincident(g2,g3)
    c: Coincident(g3,g0)
    c: Horizontal(g0)
    c: Horizontal(g2)
    c: Vertical(g1)
    c: Vertical(g3)
    c: Coincident(g0,g-6)
    c: PointOnObject(g1,g-7)
    c: Coincident(g4,g5)
    c: Coincident(g5,g6)
    c: Coincident(g6,g7)
    c: Coincident(g7,g4)
    c: Horizontal(g4)
    c: Horizontal(g6)
    c: Vertical(g5)
    c: Vertical(g7)
    c: Coincident(g4,g-5)
    c: PointOnObject(g5,g-8)
    c: Coincident(g8,g9)
    c: Coincident(g9,g10)
    c: Coincident(g10,g11)
    c: Coincident(g11,g8)
    c: Horizontal(g8)
    c: Horizontal(g10)
    c: Vertical(g9)
    c: Vertical(g11)
    c: PointOnObject(g8,g-6)
    c: PointOnObject(g9,g-7)
    c: Coincident(g12,g13)
    c: Coincident(g13,g14)
    c: Coincident(g14,g15)
    c: Coincident(g15,g12)
    c: Horizontal(g12)
    c: Horizontal(g14)
    c: Vertical(g13)
    c: Vertical(g15)
    c: PointOnObject(g12,g-8)
    c: PointOnObject(g13,g-5)
    c: Equal(g9,g1)
    c: Equal(g1,g5)
    c: Equal(g5,g15)
    c: DistanceY(g1,g1) = 8
    c: Horizontal(g8,g12)
    c: DistanceY(g-4,g8) = 4
FEATURE [PartDesign::Pocket] Pocket004
  BaseFeature = -> Pad014
  Length = 2
  Length2 = 100
  Profile = -> Sketch027
  Type = 0
FEATURE [Sketcher::SketchObject] Sketch028
  ExternalGeometry = -> [ShapeBinder004,Pocket004]
  FullyConstrained = true
  MapMode = 5
  Placement = pos=(59,0,0) rot=(0.57735,0.57735,0.57735;2.0944rad)
  Support = -> [Pocket004]
  sketch-geometry (20):
    g0: LineSegment StartX=-19.5 StartY=17.8 StartZ=0 EndX=-6.5 EndY=17.8 EndZ=0
    g1: LineSegment StartX=-6.5 StartY=17.8 StartZ=0 EndX=-6.5 EndY=11.8 EndZ=0
    g2: LineSegment StartX=-6.5 StartY=11.8 StartZ=0 EndX=-19.5 EndY=11.8 EndZ=0
    g3: LineSegment StartX=-19.5 StartY=11.8 StartZ=0 EndX=-19.5 EndY=17.8 EndZ=0
    g4: LineSegment StartX=-4.2 StartY=17.8 StartZ=0 EndX=1.6 EndY=17.8 EndZ=0
    g5: LineSegment StartX=1.6 StartY=17.8 StartZ=0 EndX=1.6 EndY=13.8 EndZ=0
    g6: LineSegment StartX=1.6 StartY=13.8 StartZ=0 EndX=-4.2 EndY=13.8 EndZ=0
    g7: LineSegment StartX=-4.2 StartY=13.8 StartZ=0 EndX=-4.2 EndY=17.8 EndZ=0
    g8: LineSegment StartX=4.5 StartY=17.8 StartZ=0 EndX=8.5 EndY=17.8 EndZ=0
    g9: LineSegment StartX=8.5 StartY=17.8 StartZ=0 EndX=8.5 EndY=13.8 EndZ=0
    g10: LineSegment StartX=8.5 StartY=13.8 StartZ=0 EndX=4.5 EndY=13.8 EndZ=0
    g11: LineSegment StartX=4.5 StartY=13.8 StartZ=0 EndX=4.5 EndY=17.8 EndZ=0
    g12: LineSegment StartX=16.5 StartY=17.8 StartZ=0 EndX=20.5 EndY=17.8 EndZ=0
    g13: LineSegment StartX=20.5 StartY=17.8 StartZ=0 EndX=20.5 EndY=13.8 EndZ=0
    g14: LineSegment StartX=20.5 StartY=13.8 StartZ=0 EndX=16.5 EndY=13.8 EndZ=0
    g15: LineSegment StartX=16.5 StartY=13.8 StartZ=0 EndX=16.5 EndY=17.8 EndZ=0
    g16: LineSegment StartX=10.5 StartY=16.6 StartZ=0 EndX=14.5 EndY=16.6 EndZ=0
    g17: LineSegment StartX=14.5 StartY=16.6 StartZ=0 EndX=14.5 EndY=15 EndZ=0
    g18: LineSegment StartX=14.5 StartY=15 StartZ=0 EndX=10.5 EndY=15 EndZ=0
    g19: LineSegment StartX=10.5 StartY=15 StartZ=0 EndX=10.5 EndY=16.6 EndZ=0
  constraints (62):
    c: Coincident(g0,g1)
    c: Coincident(g1,g2)
    c: Coincident(g2,g3)
    c: Coincident(g3,g0)
    c: Horizontal(g0)
    c: Horizontal(g2)
    c: Vertical(g1)
    c: Vertical(g3)
    c: PointOnObject(g0,g-8)
    c: Coincident(g4,g5)
    c: Coincident(g5,g6)
    c: Coincident(g6,g7)
    c: Coincident(g7,g4)
    c: Horizontal(g4)
    c: Horizontal(g6)
    c: Vertical(g5)
    c: Vertical(g7)
    c: Coincident(g8,g9)
    c: Coincident(g9,g10)
    c: Coincident(g10,g11)
    c: Coincident(g11,g8)
    c: Horizontal(g8)
    c: Horizontal(g10)
    c: Vertical(g9)
    c: Vertical(g11)
    c: PointOnObject(g8,g-8)
    c: Coincident(g12,g13)
    c: Coincident(g13,g14)
    c: Coincident(g14,g15)
    c: Coincident(g15,g12)
    c: Horizontal(g12)
    c: Horizontal(g14)
    c: Vertical(g13)
    c: Vertical(g15)
    c: PointOnObject(g12,g-8)
    c: Coincident(g16,g17)
    c: Coincident(g17,g18)
    c: Coincident(g18,g19)
    c: Coincident(g19,g16)
    c: Horizontal(g16)
    c: Horizontal(g18)
    c: Vertical(g17)
    c: Vertical(g19)
    c: DistanceY(g3,g3) = 6
    c: DistanceX(g0,g0) = 13
    c: DistanceX(g2,g-6) = 2
    c: Equal(g9,g13)
    c: DistanceY(g13,g13) = 4
    c: DistanceX(g18,g18) = 4
    c: DistanceX(g9,g18) = 2
    c: DistanceY(g17,g17) = 1.6
    c: DistanceY(g16,g12) = 1.2
    c: PointOnObject(g4,g-8)
    c: DistanceY(g7,g7) = 4
    c: DistanceX(g-3,g-3) = 4
    c: DistanceX(g13,g-4) = 0
    c: DistanceX(g-4,g14) = 0
    c: DistanceX(g-3,g10) = 0
    c: DistanceX(g9,g-3) = 0
    c: DistanceX(g-5,g5) = 1.4
    c: DistanceX(g6,g-5) = 1.4
    c: DistanceX(g-7,g-7) = 6.8
FEATURE [PartDesign::Pocket] Pocket005
  BaseFeature = -> Pocket004
  Length = 2.8
  Length2 = 100
  Profile = -> Sketch028
  Type = 0
FEATURE [Sketcher::SketchObject] Sketch029
  ExternalGeometry = -> [Pocket005]
  FullyConstrained = true
  MapMode = 5
  Placement = pos=(0,0,17.8) rot=(0,0,1;0rad)
  Support = -> [Pocket005]
  sketch-geometry (4):
    g0: LineSegment StartX=56.2 StartY=22.1 StartZ=0 EndX=56.2 EndY=-6.2 EndZ=0
    g1: LineSegment StartX=56.2 StartY=-6.2 StartZ=0 EndX=56.8 EndY=-6.2 EndZ=0
    g2: LineSegment StartX=56.8 StartY=-6.2 StartZ=0 EndX=56.8 EndY=22.1 EndZ=0
    g3: LineSegment StartX=56.2 StartY=22.1 StartZ=0 EndX=56.8 EndY=22.1 EndZ=0
  constraints (12):
    c: Coincident(g0,g1)
    c: Coincident(g1,g2)
    c: Horizontal(g1)
    c: Vertical(g0)
    c: Vertical(g2)
    c: Vertical(g-5,g0)
    c: Coincident(g3,g0)
    c: Coincident(g3,g2)
    c: Horizontal(g3)
    c: DistanceX(g3,g3) = 0.6
    c: DistanceY(g-4,g2) = 1.6
    c: DistanceY(g1,g-5) = 2
FEATURE [PartDesign::Pocket] Pocket006
  BaseFeature = -> Pocket005
  Length = 7.8
  Length2 = 100
  Profile = -> Sketch029
  Type = 0
FEATURE [Sketcher::SketchObject] Sketch030
  ExternalGeometry = -> [ShapeBinder004,Pocket006]
  FullyConstrained = true
  MapMode = 5
  Placement = pos=(0,34.5,0) rot=(0,0.707107,0.707107;3.14159rad)
  Support = -> [Pocket006]
  sketch-geometry (4):
    g0: LineSegment StartX=-44.4 StartY=16.6 StartZ=0 EndX=-31.4 EndY=16.6 EndZ=0
    g1: LineSegment StartX=-31.4 StartY=16.6 StartZ=0 EndX=-31.4 EndY=14.6 EndZ=0
    g2: LineSegment StartX=-31.4 StartY=14.6 StartZ=0 EndX=-44.4 EndY=14.6 EndZ=0
    g3: LineSegment StartX=-44.4 StartY=14.6 StartZ=0 EndX=-44.4 EndY=16.6 EndZ=0
  constraints (12):
    c: Coincident(g0,g1)
    c: Coincident(g1,g2)
    c: Coincident(g2,g3)
    c: Coincident(g3,g0)
    c: Horizontal(g0)
    c: Horizontal(g2)
    c: Vertical(g1)
    c: Vertical(g3)
    c: DistanceX(g-3,g1) = 1
    c: DistanceX(g2,g-3) = 1
    c: DistanceY(g0,g-4) = 1.2
    c: DistanceY(g1,g1) = 2
FEATURE [PartDesign::Pocket] Pocket007
  BaseFeature = -> Pocket006
  Length = 2.8
  Length2 = 100
  Profile = -> Sketch030
  Type = 0
FEATURE [Sketcher::SketchObject] Sketch031
  ExternalGeometry = -> [ShapeBinder006]
  FullyConstrained = true
  MapMode = 5
  Placement = pos=(0,0,23.6) rot=(0,0,1;0rad)
  Support = -> [Pocket002]
  sketch-geometry (28):
    g0: LineSegment StartX=-51.4 StartY=-33.8 StartZ=0 EndX=-41.6 EndY=-33.8 EndZ=0
    g1: LineSegment StartX=-40.6 StartY=-34.8 StartZ=0 EndX=-40.6 EndY=-44.6 EndZ=0
    g2: LineSegment StartX=-41.6 StartY=-45.6 StartZ=0 EndX=-51.4 EndY=-45.6 EndZ=0
    g3: LineSegment StartX=-52.4 StartY=-44.6 StartZ=0 EndX=-52.4 EndY=-34.8 EndZ=0
    g4: LineSegment StartX=-37.6 StartY=-33.8 StartZ=0 EndX=-27.8 EndY=-33.8 EndZ=0
    g5: LineSegment StartX=-26.8 StartY=-34.8 StartZ=0 EndX=-26.8 EndY=-44.6 EndZ=0
    g6: LineSegment StartX=-27.8 StartY=-45.6 StartZ=0 EndX=-37.6 EndY=-45.6 EndZ=0
    g7: LineSegment StartX=-38.6 StartY=-44.6 StartZ=0 EndX=-38.6 EndY=-34.8 EndZ=0
    g8: LineSegment StartX=-9.5 StartY=-33.8 StartZ=0 EndX=0.3 EndY=-33.8 EndZ=0
    g9: LineSegment StartX=1.3 StartY=-34.8 StartZ=0 EndX=1.3 EndY=-44.6 EndZ=0
    g10: LineSegment StartX=0.3 StartY=-45.6 StartZ=0 EndX=-9.5 EndY=-45.6 EndZ=0
    g11: LineSegment StartX=-10.5 StartY=-44.6 StartZ=0 EndX=-10.5 EndY=-34.8 EndZ=0
    g12: ArcOfCircle CenterX=-51.4 CenterY=-34.8 CenterZ=0 NormalX=0 NormalY=0 NormalZ=1 AngleXU=0 Radius=1 StartAngle=1.5708 EndAngle=3.14159
    g13: ArcOfCircle CenterX=-41.6 CenterY=-34.8 CenterZ=0 NormalX=0 NormalY=0 NormalZ=1 AngleXU=0 Radius=1 StartAngle=1.2e-15 EndAngle=1.5708
    g14: ArcOfCircle CenterX=-41.6 CenterY=-44.6 CenterZ=0 NormalX=0 NormalY=0 NormalZ=1 AngleXU=0 Radius=1 StartAngle=4.71239 EndAngle=6.28319
    g15: ArcOfCircle CenterX=-51.4 CenterY=-44.6 CenterZ=0 NormalX=0 NormalY=0 NormalZ=1 AngleXU=0 Radius=1 StartAngle=3.14159 EndAngle=4.71239
    g16: ArcOfCircle CenterX=-37.6 CenterY=-34.8 CenterZ=0 NormalX=0 NormalY=0 NormalZ=1 AngleXU=0 Radius=1 StartAngle=1.5708 EndAngle=3.14159
    g17: ArcOfCircle CenterX=-27.8 CenterY=-34.8 CenterZ=0 NormalX=0 NormalY=0 NormalZ=1 AngleXU=0 Radius=1 StartAngle=1.5e-15 EndAngle=1.5708
    g18: ArcOfCircle CenterX=-27.8 CenterY=-44.6 CenterZ=0 NormalX=0 NormalY=0 NormalZ=1 AngleXU=0 Radius=1 StartAngle=4.71239 EndAngle=6.28319
    g19: ArcOfCircle CenterX=-37.6 CenterY=-44.6 CenterZ=0 NormalX=0 NormalY=0 NormalZ=1 AngleXU=0 Radius=1 StartAngle=3.14159 EndAngle=4.71239
    g20: ArcOfCircle CenterX=-9.5 CenterY=-34.8 CenterZ=0 NormalX=0 NormalY=0 NormalZ=1 AngleXU=0 Radius=1 StartAngle=1.5708 EndAngle=3.14159
    g21: ArcOfCircle CenterX=0.3 CenterY=-34.8 CenterZ=0 NormalX=0 NormalY=0 NormalZ=1 AngleXU=0 Radius=1 StartAngle=2e-16 EndAngle=1.5708
    g22: ArcOfCircle CenterX=0.3 CenterY=-44.6 CenterZ=0 NormalX=0 NormalY=0 NormalZ=1 AngleXU=0 Radius=1 StartAngle=4.71239 EndAngle=6.28319
    g23: ArcOfCircle CenterX=-9.5 CenterY=-44.6 CenterZ=0 NormalX=0 NormalY=0 NormalZ=1 AngleXU=0 Radius=1 StartAngle=3.14159 EndAngle=4.71239
    g24: LineSegment StartX=-55 StartY=30.5 StartZ=0 EndX=55 EndY=30.5 EndZ=0
    g25: LineSegment StartX=55 StartY=30.5 StartZ=0 EndX=55 EndY=-47.5 EndZ=0
    g26: LineSegment StartX=55 StartY=-47.5 StartZ=0 EndX=-55 EndY=-47.5 EndZ=0
    g27: LineSegment StartX=-55 StartY=-47.5 StartZ=0 EndX=-55 EndY=30.5 EndZ=0
  constraints (70):
    c: Horizontal(g0)
    c: Horizontal(g2)
    c: Vertical(g1)
    c: Vertical(g3)
    c: Horizontal(g4)
    c: Horizontal(g6)
    c: Vertical(g5)
    c: Vertical(g7)
    c: Horizontal(g8)
    c: Horizontal(g10)
    c: Vertical(g9)
    c: Vertical(g11)
    c: Tangent(g0,g12) = 1.5708
    c: Tangent(g3,g12) = 1.5708
    c: Tangent(g0,g13) = 1.5708
    c: Tangent(g1,g13) = 1.5708
    c: Tangent(g1,g14) = 1.5708
    c: Tangent(g2,g14) = 1.5708
    c: Tangent(g2,g15) = 1.5708
    c: Tangent(g3,g15) = 1.5708
    c: Tangent(g4,g16) = 1.5708
    c: Tangent(g7,g16) = 1.5708
    c: Tangent(g4,g17) = 1.5708
    c: Tangent(g5,g17) = 1.5708
    c: Tangent(g5,g18) = 1.5708
    c: Tangent(g6,g18) = 1.5708
    c: Tangent(g6,g19) = 1.5708
    c: Tangent(g7,g19) = 1.5708
    c: Tangent(g8,g20) = 1.5708
    c: Tangent(g11,g20) = 1.5708
    c: Tangent(g8,g21) = 1.5708
    c: Tangent(g9,g21) = 1.5708
    c: Tangent(g9,g22) = 1.5708
    c: Tangent(g10,g22) = 1.5708
    c: Tangent(g10,g23) = 1.5708
    c: Tangent(g11,g23) = 1.5708
    c: Coincident(g24,g25)
    c: Coincident(g25,g26)
    c: Coincident(g26,g27)
    c: Coincident(g27,g24)
    c: Horizontal(g26)
    c: Vertical(g25)
    c: Vertical(g27)
    c: Coincident(g24,g-3)
    c: Coincident(g24,g-3)
    c: DistanceY(g25,g-4) = 17
    c: Equal(g0,g1)
    c: Equal(g1,g4)
    c: Equal(g4,g5)
    c: Equal(g5,g8)
    c: Equal(g8,g9)
    c: Equal(g3,g2)
    c: Equal(g2,g7)
    c: Equal(g7,g6)
    c: Equal(g6,g11)
    c: Equal(g11,g10)
    c: Equal(g10,g9)
    c: Vertical(g14,g13)
    c: Vertical(g18,g17)
    c: Vertical(g21,g22)
    c: Horizontal(g20,g16)
    c: Horizontal(g16,g12)
    c: Equal(g13,g17)
    c: Equal(g17,g21)
    c: Radius(g21) = 1
    c: DistanceX(g26,g3) = 2.6
    c: DistanceX(g26,g7) = 16.4
    c: DistanceX(g26,g11) = 44.5
    c: DistanceY(g26,g2) = 1.9
    c: DistanceY(g2,g0) = 11.8
FEATURE [PartDesign::Pocket] Pocket008
  BaseFeature = -> Pocket002
  Length = 5
  Length2 = 100
  Profile = -> Sketch031
  Type = 1
FEATURE [Sketcher::SketchObject] Sketch032
  ExternalGeometry = -> [Pocket007]
  FullyConstrained = true
  MapMode = 5
  Placement = pos=(0,-47.7,0) rot=(0,0.707107,0.707107;3.14159rad)
  Support = -> [Pocket007]
  sketch-geometry (2):
    g0: Circle CenterX=-48.2 CenterY=4 CenterZ=0 NormalX=0 NormalY=0 NormalZ=1 AngleXU=0 Radius=1.2
    g1: Circle CenterX=-43.2 CenterY=4 CenterZ=0 NormalX=0 NormalY=0 NormalZ=1 AngleXU=0 Radius=1.2
  constraints (6):
    c: Horizontal(g0,g1)
    c: Equal(g1,g0)
    c: Radius(g1) = 1.2
    c: DistanceX(g-3,g0) = 4
    c: DistanceX(g0,g1) = 5
    c: DistanceY(g-3,g0) = 2
FEATURE [PartDesign::Pocket] Pocket009
  BaseFeature = -> Pocket007
  Length = 2.8
  Length2 = 100
  Profile = -> Sketch032
  Type = 0
FEATURE [Sketcher::SketchObject] Sketch033
  FullyConstrained = true
  MapMode = 5
  Support = -> [XY_Plane004]
  sketch-geometry (4):
    g0: LineSegment StartX=-6.2 StartY=6.2 StartZ=0 EndX=6.2 EndY=6.2 EndZ=0
    g1: LineSegment StartX=6.2 StartY=6.2 StartZ=0 EndX=6.2 EndY=-6.2 EndZ=0
    g2: LineSegment StartX=6.2 StartY=-6.2 StartZ=0 EndX=-6.2 EndY=-6.2 EndZ=0
    g3: LineSegment StartX=-6.2 StartY=-6.2 StartZ=0 EndX=-6.2 EndY=6.2 EndZ=0
  constraints (10):
    c: Coincident(g0,g1)
    c: Coincident(g1,g2)
    c: Coincident(g2,g3)
    c: Coincident(g3,g0)
    c: Horizontal(g2)
    c: Vertical(g1)
    c: Symmetric(g0,g0,g-2)
    c: Symmetric(g0,g2,g-1)
    c: Equal(g0,g3)
    c: DistanceY(g3,g3) = 12.4
FEATURE [PartDesign::Pad] Pad015
  Direction = (1,1,1)
  Length = 5.8
  Length2 = 100
  Profile = -> Sketch033
  Type = 0
FEATURE [Sketcher::SketchObject] Sketch034
  FullyConstrained = true
  MapMode = 5
  Placement = pos=(0,0,5.8) rot=(0,0,1;0rad)
  Support = -> [Pad015]
  sketch-geometry (8):
    g0: LineSegment StartX=-4.5 StartY=5.5 StartZ=0 EndX=4.5 EndY=5.5 EndZ=0
    g1: LineSegment StartX=5.5 StartY=4.5 StartZ=0 EndX=5.5 EndY=-4.5 EndZ=0
    g2: LineSegment StartX=4.5 StartY=-5.5 StartZ=0 EndX=-4.5 EndY=-5.5 EndZ=0
    g3: LineSegment StartX=-5.5 StartY=-4.5 StartZ=0 EndX=-5.5 EndY=4.5 EndZ=0
    g4: ArcOfCircle CenterX=-4.5 CenterY=4.5 CenterZ=0 NormalX=0 NormalY=0 NormalZ=1 AngleXU=0 Radius=1 StartAngle=1.5708 EndAngle=3.14159
    g5: ArcOfCircle CenterX=4.5 CenterY=4.5 CenterZ=0 NormalX=0 NormalY=0 NormalZ=1 AngleXU=0 Radius=1 StartAngle=0 EndAngle=1.5708
    g6: ArcOfCircle CenterX=4.5 CenterY=-4.5 CenterZ=0 NormalX=0 NormalY=0 NormalZ=1 AngleXU=0 Radius=1 StartAngle=4.71239 EndAngle=6.28319
    g7: ArcOfCircle CenterX=-4.5 CenterY=-4.5 CenterZ=0 NormalX=0 NormalY=0 NormalZ=1 AngleXU=0 Radius=1 StartAngle=3.14159 EndAngle=4.71239
  constraints (18):
    c: Horizontal(g0)
    c: Vertical(g3)
    c: Tangent(g0,g4) = 1.5708
    c: Tangent(g3,g4) = 1.5708
    c: Tangent(g0,g5) = 1.5708
    c: Tangent(g1,g5) = 1.5708
    c: Tangent(g1,g6) = 1.5708
    c: Tangent(g2,g6) = 1.5708
    c: Tangent(g2,g7) = 1.5708
    c: Tangent(g3,g7) = 1.5708
    c: Equal(g5,g4)
    c: Equal(g4,g7)
    c: Equal(g7,g6)
    c: Radius(g5) = 1
    c: Equal(g3,g0)
    c: Symmetric(g1,g1,g-1)
    c: Symmetric(g2,g2,g-2)
    c: DistanceY(g2,g0) = 11
FEATURE [PartDesign::Pad] Pad016
  BaseFeature = -> Pad015
  Direction = (1,1,1)
  Length = 2.6
  Length2 = 100
  Profile = -> Sketch034
  Type = 0
FEATURE [Sketcher::SketchObject] Sketch035
  FullyConstrained = true
  MapMode = 5
  Placement = pos=(0,0,8.4) rot=(0,0,1;0rad)
  Support = -> [Pad016]
  sketch-geometry (1):
    g0: Circle CenterX=0 CenterY=0 CenterZ=0 NormalX=0 NormalY=0 NormalZ=1 AngleXU=0 Radius=3
  constraints (2):
    c: Coincident(g0,g-1)
    c: Radius(g0) = 3
FEATURE [PartDesign::Pocket] Pocket010
  BaseFeature = -> Pad016
  Length = 0.6
  Length2 = 100
  Profile = -> Sketch035
  Type = 0
FEATURE [Sketcher::SketchObject] Sketch036
  FullyConstrained = true
  MapMode = 5
  Placement = pos=(0,0,0) rot=(1,0,0;3.14159rad)
  Support = -> [Pocket010]
  sketch-geometry (1):
    g0: Circle CenterX=0 CenterY=0 CenterZ=0 NormalX=0 NormalY=0 NormalZ=1 AngleXU=0 Radius=4
  constraints (2):
    c: Coincident(g0,g-1)
    c: Radius(g0) = 4
FEATURE [PartDesign::Pocket] Pocket011
  BaseFeature = -> Pocket010
  Length = 2
  Length2 = 100
  Profile = -> Sketch036
  Type = 0
FEATURE [Sketcher::SketchObject] Sketch037
  ExternalGeometry = -> [Pocket009]
  FullyConstrained = true
  MapMode = 5
  Placement = pos=(0,0,17.8) rot=(0,0,1;0rad)
  Support = -> [Pocket009]
  sketch-geometry (16):
    g0: LineSegment StartX=-58 StartY=34.5 StartZ=0 EndX=-48 EndY=34.5 EndZ=0
    g1: LineSegment StartX=-48 StartY=34.5 StartZ=0 EndX=-48 EndY=26.5 EndZ=0
    g2: LineSegment StartX=-48 StartY=26.5 StartZ=0 EndX=-58 EndY=26.5 EndZ=0
    g3: LineSegment StartX=-58 StartY=26.5 StartZ=0 EndX=-58 EndY=34.5 EndZ=0
    g4: LineSegment StartX=59 StartY=34.5 StartZ=0 EndX=49 EndY=34.5 EndZ=0
    g5: LineSegment StartX=49 StartY=34.5 StartZ=0 EndX=49 EndY=26.5 EndZ=0
    g6: LineSegment StartX=49 StartY=26.5 StartZ=0 EndX=59 EndY=26.5 EndZ=0
    g7: LineSegment StartX=59 StartY=26.5 StartZ=0 EndX=59 EndY=34.5 EndZ=0
    g8: LineSegment StartX=-58 StartY=-50.5 StartZ=0 EndX=-48 EndY=-50.5 EndZ=0
    g9: LineSegment StartX=-48 StartY=-50.5 StartZ=0 EndX=-48 EndY=-42.5 EndZ=0
    g10: LineSegment StartX=-48 StartY=-42.5 StartZ=0 EndX=-58 EndY=-42.5 EndZ=0
    g11: LineSegment StartX=-58 StartY=-42.5 StartZ=0 EndX=-58 EndY=-50.5 EndZ=0
    g12: LineSegment StartX=59 StartY=-50.5 StartZ=0 EndX=49 EndY=-50.5 EndZ=0
    g13: LineSegment StartX=49 StartY=-50.5 StartZ=0 EndX=49 EndY=-42.5 EndZ=0
    g14: LineSegment StartX=49 StartY=-42.5 StartZ=0 EndX=59 EndY=-42.5 EndZ=0
    g15: LineSegment StartX=59 StartY=-42.5 StartZ=0 EndX=59 EndY=-50.5 EndZ=0
  constraints (44):
    c: Coincident(g0,g1)
    c: Coincident(g1,g2)
    c: Coincident(g2,g3)
    c: Coincident(g3,g0)
    c: Horizontal(g0)
    c: Horizontal(g2)
    c: Vertical(g1)
    c: Vertical(g3)
    c: Coincident(g0,g-3)
    c: Coincident(g4,g5)
    c: Coincident(g5,g6)
    c: Coincident(g6,g7)
    c: Coincident(g7,g4)
    c: Horizontal(g4)
    c: Horizontal(g6)
    c: Vertical(g5)
    c: Vertical(g7)
    c: Coincident(g4,g-3)
    c: Coincident(g8,g9)
    c: Coincident(g9,g10)
    c: Coincident(g10,g11)
    c: Coincident(g11,g8)
    c: Horizontal(g8)
    c: Horizontal(g10)
    c: Vertical(g9)
    c: Vertical(g11)
    c: Coincident(g8,g-4)
    c: Coincident(g12,g13)
    c: Coincident(g13,g14)
    c: Coincident(g14,g15)
    c: Coincident(g15,g12)
    c: Horizontal(g12)
    c: Horizontal(g14)
    c: Vertical(g13)
    c: Vertical(g15)
    c: Coincident(g12,g-4)
    c: Equal(g3,g7)
    c: Equal(g7,g15)
    c: Equal(g15,g11)
    c: Equal(g0,g4)
    c: Equal(g4,g12)
    c: Equal(g12,g8)
    c: DistanceY(g3,g3) = 8
    c: DistanceX(g0,g0) = 10
FEATURE [PartDesign::Pocket] Pocket012
  BaseFeature = -> Pocket009
  Length = 5
  Length2 = 100
  Profile = -> Sketch037
  Type = 0
FEATURE [Sketcher::SketchObject] Sketch038
  ExternalGeometry = -> [Pocket008]
  FullyConstrained = true
  MapMode = 5
  Placement = pos=(0,0,17.8) rot=(1,0,0;3.14159rad)
  Support = -> [Pocket008]
  sketch-geometry (24):
    g0: LineSegment StartX=-58 StartY=50.5 StartZ=0 EndX=-48.2 EndY=50.5 EndZ=0
    g1: LineSegment StartX=-48.2 StartY=50.5 StartZ=0 EndX=-48.2 EndY=47.7 EndZ=0
    g2: LineSegment StartX=-55.2 StartY=42.7 StartZ=0 EndX=-58 EndY=42.7 EndZ=0
    g3: LineSegment StartX=-58 StartY=42.7 StartZ=0 EndX=-58 EndY=50.5 EndZ=0
    g4: LineSegment StartX=59 StartY=50.5 StartZ=0 EndX=49.2 EndY=50.5 EndZ=0
    g5: LineSegment StartX=49.2 StartY=50.5 StartZ=0 EndX=49.2 EndY=47.7 EndZ=0
    g6: LineSegment StartX=56.2 StartY=42.7 StartZ=0 EndX=59 EndY=42.7 EndZ=0
    g7: LineSegment StartX=59 StartY=42.7 StartZ=0 EndX=59 EndY=50.5 EndZ=0
    g8: LineSegment StartX=59 StartY=-34.5 StartZ=0 EndX=49.2 EndY=-34.5 EndZ=0
    g9: LineSegment StartX=49.2 StartY=-34.5 StartZ=0 EndX=49.2 EndY=-31.7 EndZ=0
    g10: LineSegment StartX=56.2 StartY=-26.7 StartZ=0 EndX=59 EndY=-26.7 EndZ=0
    g11: LineSegment StartX=59 StartY=-26.7 StartZ=0 EndX=59 EndY=-34.5 EndZ=0
    g12: LineSegment StartX=-58 StartY=-34.5 StartZ=0 EndX=-48.2 EndY=-34.5 EndZ=0
    g13: LineSegment StartX=-48.2 StartY=-34.5 StartZ=0 EndX=-48.2 EndY=-31.7 EndZ=0
    g14: LineSegment StartX=-55.2 StartY=-26.7 StartZ=0 EndX=-58 EndY=-26.7 EndZ=0
    g15: LineSegment StartX=-58 StartY=-26.7 StartZ=0 EndX=-58 EndY=-34.5 EndZ=0
    g16: LineSegment StartX=-55.2 StartY=-31.7 StartZ=0 EndX=-48.2 EndY=-31.7 EndZ=0
    g17: LineSegment StartX=-55.2 StartY=-26.7 StartZ=0 EndX=-55.2 EndY=-31.7 EndZ=0
    g18: LineSegment StartX=-55.2 StartY=47.7 StartZ=0 EndX=-48.2 EndY=47.7 EndZ=0
    g19: LineSegment StartX=-55.2 StartY=42.7 StartZ=0 EndX=-55.2 EndY=47.7 EndZ=0
    g20: LineSegment StartX=56.2 StartY=47.7 StartZ=0 EndX=49.2 EndY=47.7 EndZ=0
    g21: LineSegment StartX=56.2 StartY=42.7 StartZ=0 EndX=56.2 EndY=47.7 EndZ=0
    g22: LineSegment StartX=56.2 StartY=-31.7 StartZ=0 EndX=49.2 EndY=-31.7 EndZ=0
    g23: LineSegment StartX=56.2 StartY=-26.7 StartZ=0 EndX=56.2 EndY=-31.7 EndZ=0
  constraints (64):
    c: Coincident(g0,g1)
    c: Coincident(g2,g3)
    c: Coincident(g3,g0)
    c: Horizontal(g0)
    c: Horizontal(g2)
    c: Vertical(g1)
    c: Vertical(g3)
    c: Coincident(g0,g-3)
    c: Coincident(g4,g5)
    c: Coincident(g6,g7)
    c: Coincident(g7,g4)
    c: Horizontal(g4)
    c: Horizontal(g6)
    c: Vertical(g5)
    c: Vertical(g7)
    c: Coincident(g4,g-3)
    c: Coincident(g8,g9)
    c: Coincident(g10,g11)
    c: Coincident(g11,g8)
    c: Horizontal(g8)
    c: Horizontal(g10)
    c: Vertical(g9)
    c: Vertical(g11)
    c: Coincident(g8,g-4)
    c: Coincident(g12,g13)
    c: Coincident(g14,g15)
    c: Coincident(g15,g12)
    c: Horizontal(g12)
    c: Horizontal(g14)
    c: Vertical(g13)
    c: Vertical(g15)
    c: Coincident(g12,g-4)
    c: Equal(g7,g11)
    c: Equal(g11,g15)
    c: Equal(g15,g3)
    c: DistanceX(g8,g8) = 9.8
    c: DistanceY(g11,g11) = 7.8
    c: Coincident(g17,g16)
    c: Horizontal(g16)
    c: Vertical(g17)
    c: Coincident(g16,g-6)
    c: Coincident(g19,g18)
    c: Horizontal(g18)
    c: Vertical(g19)
    c: Coincident(g18,g-5)
    c: Coincident(g21,g20)
    c: Horizontal(g20)
    c: Vertical(g21)
    c: Coincident(g20,g-5)
    c: Coincident(g23,g22)
    c: Horizontal(g22)
    c: Vertical(g23)
    c: Coincident(g22,g-6)
    c: Coincident(g23,g10)
    c: Coincident(g22,g9)
    c: Coincident(g16,g13)
    c: Coincident(g17,g14)
    c: Coincident(g18,g1)
    c: Coincident(g19,g2)
    c: Coincident(g20,g5)
    c: Coincident(g21,g6)
    c: Equal(g12,g0)
    c: Equal(g0,g4)
    c: Equal(g4,g8)
FEATURE [PartDesign::Pad] Pad017
  BaseFeature = -> Pocket008
  Direction = (1,1,1)
  Length = 5
  Length2 = 100
  Profile = -> Sketch038
  Type = 0
FEATURE [Sketcher::SketchObject] Sketch043
  ExternalGeometry = -> [Pocket012]
  FullyConstrained = true
  MapMode = 5
  Placement = pos=(0,-50.5,0) rot=(1,0,0;1.5708rad)
  Support = -> [Pocket012]
  sketch-geometry (8):
    g0: LineSegment StartX=-48 StartY=12.8 StartZ=0 EndX=-46.6 EndY=12.8 EndZ=0
    g1: LineSegment StartX=-46.6 StartY=12.8 StartZ=0 EndX=-46.6 EndY=14.4 EndZ=0
    g2: LineSegment StartX=-46.6 StartY=14.4 StartZ=0 EndX=-48 EndY=16 EndZ=0
    g3: LineSegment StartX=-48 StartY=16 StartZ=0 EndX=-48 EndY=12.8 EndZ=0
    g4: LineSegment StartX=49 StartY=12.8 StartZ=0 EndX=47.6 EndY=12.8 EndZ=0
    g5: LineSegment StartX=47.6 StartY=12.8 StartZ=0 EndX=47.6 EndY=14.4 EndZ=0
    g6: LineSegment StartX=47.6 StartY=14.4 StartZ=0 EndX=49 EndY=16 EndZ=0
    g7: LineSegment StartX=49 StartY=16 StartZ=0 EndX=49 EndY=12.8 EndZ=0
  constraints (22):
    c: Coincident(g0,g-3)
    c: Horizontal(g0)
    c: Coincident(g1,g0)
    c: Vertical(g1)
    c: Coincident(g2,g1)
    c: PointOnObject(g2,g-3)
    c: Coincident(g3,g2)
    c: Coincident(g3,g0)
    c: Coincident(g4,g-4)
    c: Horizontal(g4)
    c: Coincident(g5,g4)
    c: Vertical(g5)
    c: Coincident(g6,g5)
    c: PointOnObject(g6,g-4)
    c: Coincident(g7,g6)
    c: Coincident(g7,g4)
    c: Equal(g0,g4)
    c: Equal(g1,g5)
    c: Equal(g3,g7)
    c: DistanceX(g0,g0) = 1.4
    c: DistanceY(g1,g1) = 1.6
    c: DistanceY(g3,g3) = 3.2
FEATURE [PartDesign::Pocket] Pocket015
  BaseFeature = -> Pocket012
  Length = 5
  Length2 = 100
  Profile = -> Sketch043
  Type = 1
FEATURE [Sketcher::SketchObject] Sketch044
  ExternalGeometry = -> [Pad017]
  FullyConstrained = true
  MapMode = 5
  Placement = pos=(-48.2,0,0) rot=(0.57735,0.57735,0.57735;2.0944rad)
  Support = -> [Pad017]
  sketch-geometry (8):
    g0: LineSegment StartX=-50.5 StartY=12.8 StartZ=0 EndX=-47.7 EndY=12.8 EndZ=0
    g1: LineSegment StartX=-47.7 StartY=12.8 StartZ=0 EndX=-47.7 EndY=16 EndZ=0
    g2: LineSegment StartX=-47.7 StartY=16 StartZ=0 EndX=-50.5 EndY=16 EndZ=0
    g3: LineSegment StartX=-50.5 StartY=16 StartZ=0 EndX=-50.5 EndY=12.8 EndZ=0
    g4: LineSegment StartX=34.5 StartY=12.8 StartZ=0 EndX=31.7 EndY=12.8 EndZ=0
    g5: LineSegment StartX=31.7 StartY=12.8 StartZ=0 EndX=31.7 EndY=16 EndZ=0
    g6: LineSegment StartX=31.7 StartY=16 StartZ=0 EndX=34.5 EndY=16 EndZ=0
    g7: LineSegment StartX=34.5 StartY=16 StartZ=0 EndX=34.5 EndY=12.8 EndZ=0
  constraints (22):
    c: Coincident(g0,g1)
    c: Coincident(g1,g2)
    c: Coincident(g2,g3)
    c: Coincident(g3,g0)
    c: Horizontal(g0)
    c: Horizontal(g2)
    c: Vertical(g1)
    c: Vertical(g3)
    c: Coincident(g0,g-3)
    c: Coincident(g4,g5)
    c: Coincident(g5,g6)
    c: Coincident(g6,g7)
    c: Coincident(g7,g4)
    c: Horizontal(g4)
    c: Horizontal(g6)
    c: Vertical(g5)
    c: Vertical(g7)
    c: Coincident(g4,g-4)
    c: Equal(g7,g1)
    c: Equal(g4,g0)
    c: DistanceX(g0,g0) = 2.8
    c: DistanceY(g3,g3) = 3.2
FEATURE [PartDesign::Pad] Pad018
  BaseFeature = -> Pad017
  Direction = (1,1,1)
  Length = 1.4
  Length2 = 100
  Profile = -> Sketch044
  Type = 0
FEATURE [Sketcher::SketchObject] Sketch045
  ExternalGeometry = -> [Pad018]
  FullyConstrained = true
  MapMode = 5
  Placement = pos=(49.2,0,0) rot=(0.57735,-0.57735,-0.57735;2.0944rad)
  Support = -> [Pad018]
  sketch-geometry (8):
    g0: LineSegment StartX=-34.5 StartY=12.8 StartZ=0 EndX=-31.7 EndY=12.8 EndZ=0
    g1: LineSegment StartX=-31.7 StartY=12.8 StartZ=0 EndX=-31.7 EndY=16 EndZ=0
    g2: LineSegment StartX=-31.7 StartY=16 StartZ=0 EndX=-34.5 EndY=16 EndZ=0
    g3: LineSegment StartX=-34.5 StartY=16 StartZ=0 EndX=-34.5 EndY=12.8 EndZ=0
    g4: LineSegment StartX=50.5 StartY=12.8 StartZ=0 EndX=47.7 EndY=12.8 EndZ=0
    g5: LineSegment StartX=47.7 StartY=12.8 StartZ=0 EndX=47.7 EndY=16 EndZ=0
    g6: LineSegment StartX=47.7 StartY=16 StartZ=0 EndX=50.5 EndY=16 EndZ=0
    g7: LineSegment StartX=50.5 StartY=16 StartZ=0 EndX=50.5 EndY=12.8 EndZ=0
  constraints (22):
    c: Coincident(g0,g1)
    c: Coincident(g1,g2)
    c: Coincident(g2,g3)
    c: Coincident(g3,g0)
    c: Horizontal(g0)
    c: Horizontal(g2)
    c: Vertical(g1)
    c: Vertical(g3)
    c: Coincident(g0,g-4)
    c: Coincident(g4,g5)
    c: Coincident(g5,g6)
    c: Coincident(g6,g7)
    c: Coincident(g7,g4)
    c: Horizontal(g4)
    c: Horizontal(g6)
    c: Vertical(g5)
    c: Vertical(g7)
    c: Coincident(g4,g-3)
    c: Equal(g0,g4)
    c: Equal(g5,g1)
    c: DistanceX(g0,g0) = 2.8
    c: DistanceY(g3,g3) = 3.2
FEATURE [PartDesign::Pad] Pad019
  BaseFeature = -> Pad018
  Direction = (1,1,1)
  Length = 1.4
  Length2 = 100
  Profile = -> Sketch045
  Type = 0
FEATURE [Sketcher::SketchObject] Sketch046
  ExternalGeometry = -> [Pad019]
  FullyConstrained = true
  MapMode = 5
  Placement = pos=(0,-50.5,0) rot=(1,0,0;1.5708rad)
  Support = -> [Pad019]
  sketch-geometry (6):
    g0: LineSegment StartX=-48.2 StartY=16 StartZ=0 EndX=-46.8 EndY=16 EndZ=0
    g1: LineSegment StartX=-46.8 StartY=16 StartZ=0 EndX=-46.8 EndY=14.4 EndZ=0
    g2: LineSegment StartX=-46.8 StartY=14.4 StartZ=0 EndX=-48.2 EndY=16 EndZ=0
    g3: LineSegment StartX=47.8 StartY=16 StartZ=0 EndX=49.2 EndY=16 EndZ=0
    g4: LineSegment StartX=47.8 StartY=16 StartZ=0 EndX=47.8 EndY=14.4 EndZ=0
    g5: LineSegment StartX=47.8 StartY=14.4 StartZ=0 EndX=49.2 EndY=16 EndZ=0
  constraints (14):
    c: Coincident(g0,g-3)
    c: Coincident(g0,g-3)
    c: Coincident(g1,g0)
    c: Vertical(g1)
    c: Coincident(g2,g1)
    c: Coincident(g2,g0)
    c: DistanceY(g1,g1) = 1.6
    c: Coincident(g3,g-4)
    c: Coincident(g3,g-4)
    c: Coincident(g4,g3)
    c: Vertical(g4)
    c: Coincident(g5,g4)
    c: Coincident(g5,g3)
    c: Equal(g4,g1)
FEATURE [PartDesign::Pocket] Pocket016
  BaseFeature = -> Pad019
  Length = 5
  Length2 = 100
  Profile = -> Sketch046
  Type = 1
FEATURE [PartDesign::Chamfer] Chamfer
  Angle = 45
  Base = -> Pocket011 [Edge40]
  BaseFeature = -> Pocket011
  ChamferType = 0
  FlipDirection = false
  Size = 0.4
  Size2 = 1
  SupportTransform = false
FEATURE [PartDesign::Fillet] Fillet
  Base = -> Chamfer [Edge5,Edge3,Edge2,Edge4,Edge6,Face1,Edge8,Edge9,Edge7]
  BaseFeature = -> Chamfer
  Radius = 0.6
  SupportTransform = false
FEATURE [PartDesign::Body] Body004  label="Button-Cap"
  Group = -> [Sketch033,Pad015,Sketch034,Pad016,Sketch035,Pocket010,Sketch036,Pocket011,Chamfer,Fillet]
  Origin = -> Origin004
  Placement = pos=(-4.6,-39.7,15.8) rot=(0,0,1;0rad)
  Tip = -> Fillet
FEATURE [Sketcher::SketchObject] Sketch049
  FullyConstrained = true
  MapMode = 5
  Placement = pos=(0,0,0) rot=(0.57735,0.57735,0.57735;2.0944rad)
  Support = -> [YZ_Plane006]
  sketch-geometry (4):
    g0: LineSegment StartX=-8.5 StartY=3.8 StartZ=0 EndX=8.5 EndY=3.8 EndZ=0
    g1: LineSegment StartX=8.5 StartY=3.8 StartZ=0 EndX=8.5 EndY=-3.8 EndZ=0
    g2: LineSegment StartX=8.5 StartY=-3.8 StartZ=0 EndX=-8.5 EndY=-3.8 EndZ=0
    g3: LineSegment StartX=-8.5 StartY=-3.8 StartZ=0 EndX=-8.5 EndY=3.8 EndZ=0
  constraints (10):
    c: Coincident(g0,g1)
    c: Coincident(g1,g2)
    c: Coincident(g2,g3)
    c: Coincident(g3,g0)
    c: Horizontal(g0)
    c: Vertical(g3)
    c: Symmetric(g0,g1,g-1)
    c: DistanceY(g3,g3) = 7.6
    c: Symmetric(g2,g1,g-2)
    c: DistanceX(g2,g2) = 17
FEATURE [PartDesign::Pad] Pad022
  Direction = (1,1,1)
  Length = 0.8
  Length2 = 100
  Placement = pos=(0,0,0) rot=(0.57735,0.57735,0.57735;2.0944rad)
  Profile = -> Sketch049
  Type = 0
FEATURE [Sketcher::SketchObject] Sketch050
  ExternalGeometry = -> [Pad022]
  FullyConstrained = true
  MapMode = 5
  Placement = pos=(0.8,-2e-16,2e-16) rot=(0.57735,0.57735,0.57735;2.0944rad)
  Support = -> [Pad022]
  sketch-geometry (8):
    g0: LineSegment StartX=-7.5 StartY=3.8 StartZ=0 EndX=-4.5 EndY=3.8 EndZ=0
    g1: LineSegment StartX=-4.5 StartY=3.8 StartZ=0 EndX=-4.5 EndY=0.2 EndZ=0
    g2: LineSegment StartX=-4.5 StartY=0.2 StartZ=0 EndX=-7.5 EndY=0.2 EndZ=0
    g3: LineSegment StartX=-7.5 StartY=0.2 StartZ=0 EndX=-7.5 EndY=3.8 EndZ=0
    g4: LineSegment StartX=4.5 StartY=3.8 StartZ=0 EndX=7.5 EndY=3.8 EndZ=0
    g5: LineSegment StartX=7.5 StartY=3.8 StartZ=0 EndX=7.5 EndY=0.2 EndZ=0
    g6: LineSegment StartX=7.5 StartY=0.2 StartZ=0 EndX=4.5 EndY=0.2 EndZ=0
    g7: LineSegment StartX=4.5 StartY=0.2 StartZ=0 EndX=4.5 EndY=3.8 EndZ=0
  constraints (24):
    c: Coincident(g0,g1)
    c: Coincident(g1,g2)
    c: Coincident(g2,g3)
    c: Coincident(g3,g0)
    c: Horizontal(g0)
    c: Horizontal(g2)
    c: Vertical(g1)
    c: Vertical(g3)
    c: PointOnObject(g0,g-3)
    c: Coincident(g4,g5)
    c: Coincident(g5,g6)
    c: Coincident(g6,g7)
    c: Coincident(g7,g4)
    c: Horizontal(g4)
    c: Horizontal(g6)
    c: Vertical(g5)
    c: Vertical(g7)
    c: PointOnObject(g4,g-3)
    c: Equal(g0,g4)
    c: Equal(g1,g5)
    c: DistanceX(g0,g0) = 3
    c: DistanceY(g3,g3) = 3.6
    c: DistanceX(g-3,g0) = 1
    c: DistanceX(g4,g-3) = 1
FEATURE [PartDesign::Pad] Pad023
  BaseFeature = -> Pad022
  Direction = (1,1,1)
  Length = 3
  Length2 = 100
  Placement = pos=(0,0,0) rot=(0.57735,0.57735,0.57735;2.0944rad)
  Profile = -> Sketch050
  Type = 0
FEATURE [Sketcher::SketchObject] Sketch051
  ExternalGeometry = -> [Pad023]
  FullyConstrained = true
  MapMode = 5
  Placement = pos=(0.8,-2e-16,2e-16) rot=(0.57735,0.57735,0.57735;2.0944rad)
  Support = -> [Pad023]
  sketch-geometry (4):
    g0: LineSegment StartX=-2 StartY=2.6 StartZ=0 EndX=2 EndY=2.6 EndZ=0
    g1: LineSegment StartX=2 StartY=2.6 StartZ=0 EndX=2 EndY=1 EndZ=0
    g2: LineSegment StartX=2 StartY=1 StartZ=0 EndX=-2 EndY=1 EndZ=0
    g3: LineSegment StartX=-2 StartY=1 StartZ=0 EndX=-2 EndY=2.6 EndZ=0
  constraints (11):
    c: Coincident(g0,g1)
    c: Coincident(g1,g2)
    c: Coincident(g2,g3)
    c: Coincident(g3,g0)
    c: Horizontal(g0)
    c: Vertical(g1)
    c: Vertical(g3)
    c: Symmetric(g2,g1,g-2)
    c: DistanceX(g0,g0) = 4
    c: DistanceY(g3,g3) = 1.6
    c: DistanceY(g0,g-3) = 1.2
FEATURE [PartDesign::Pocket] Pocket017
  BaseFeature = -> Pad023
  Length = 5
  Length2 = 100
  Placement = pos=(0,0,0) rot=(0.57735,0.57735,0.57735;2.0944rad)
  Profile = -> Sketch051
  Type = 1
FEATURE [PartDesign::Body] Body006  label="Button-Reset"
  Group = -> [Sketch049,Pad022,Sketch050,Pad023,Sketch051,Pocket017]
  Origin = -> Origin006
  Placement = pos=(55.8,12.5,14) rot=(0,0,1;0rad)
  Tip = -> Pocket017
FEATURE [Sketcher::SketchObject] Sketch052  label="PWRBTN_OUTLINE"
  AttachmentOffset = pos=(0,0,56.6) rot=(0,0,1;0rad)
  ExternalGeometry = -> [Sketch]
  FullyConstrained = true
  MapMode = 5
  Placement = pos=(56.6,-1.26e-14,1.26e-14) rot=(0.57735,0.57735,0.57735;2.0944rad)
  Support = -> [YZ_Plane]
  sketch-geometry (12):
    g0: LineSegment StartX=-4.7 StartY=17.8 StartZ=0 EndX=2.1 EndY=17.8 EndZ=0
    g1: LineSegment StartX=2.1 StartY=17.8 StartZ=0 EndX=2.1 EndY=15 EndZ=0
    g2: LineSegment StartX=2.1 StartY=15 StartZ=0 EndX=-4.7 EndY=15 EndZ=0
    g3: LineSegment StartX=-4.7 StartY=15 StartZ=0 EndX=-4.7 EndY=17.8 EndZ=0
    g4: LineSegment StartX=-2.8 StartY=16.2 StartZ=0 EndX=-1.5 EndY=16.2 EndZ=0
    g5: LineSegment StartX=-1.5 StartY=16.2 StartZ=0 EndX=-1.5 EndY=15.2 EndZ=0
    g6: LineSegment StartX=-1.5 StartY=15.2 StartZ=0 EndX=-2.8 EndY=15.2 EndZ=0
    g7: LineSegment StartX=-2.8 StartY=15.2 StartZ=0 EndX=-2.8 EndY=16.2 EndZ=0
    g8: LineSegment StartX=-1.1 StartY=16.2 StartZ=0 EndX=0.2 EndY=16.2 EndZ=0
    g9: LineSegment StartX=0.2 StartY=16.2 StartZ=0 EndX=0.2 EndY=15.2 EndZ=0
    g10: LineSegment StartX=0.2 StartY=15.2 StartZ=0 EndX=-1.1 EndY=15.2 EndZ=0
    g11: LineSegment StartX=-1.1 StartY=15.2 StartZ=0 EndX=-1.1 EndY=16.2 EndZ=0
  constraints (36):
    c: Coincident(g0,g1)
    c: Coincident(g1,g2)
    c: Coincident(g2,g3)
    c: Coincident(g3,g0)
    c: Horizontal(g0)
    c: Horizontal(g2)
    c: Vertical(g1)
    c: Vertical(g3)
    c: DistanceX(g2,g2) = 6.8
    c: DistanceY(g3,g3) = 2.8
    c: Coincident(g4,g5)
    c: Coincident(g5,g6)
    c: Coincident(g6,g7)
    c: Coincident(g7,g4)
    c: Horizontal(g4)
    c: Horizontal(g6)
    c: Vertical(g5)
    c: Vertical(g7)
    c: Coincident(g8,g9)
    c: Coincident(g9,g10)
    c: Coincident(g10,g11)
    c: Coincident(g11,g8)
    c: Horizontal(g8)
    c: Horizontal(g10)
    c: Vertical(g9)
    c: Vertical(g11)
    c: Equal(g4,g8)
    c: Equal(g5,g9)
    c: DistanceY(g7,g7) = 1
    c: DistanceX(g4,g4) = 1.3
    c: DistanceX(g6,g1) = 4.9
    c: DistanceX(g0,g8) = 4.9
    c: Horizontal(g10,g5)
    c: DistanceY(g2,g6) = 0.2
    c: DistanceX(g1,g-3) = 28.4
    c: DistanceY(g-1,g0) = 17.8
FEATURE [PartDesign::Body] Body
  Group = -> [Sketch,Sketch008,Sketch052]
  Origin = -> Origin
FEATURE [PartDesign::ShapeBinder] ShapeBinder009
  Support = -> [Sketch052]
  TraceSupport = false
FEATURE [Sketcher::SketchObject] Sketch047
  AttachmentOffset = pos=(0,0,56.6) rot=(0,0,1;0rad)
  ExternalGeometry = -> [ShapeBinder009]
  FullyConstrained = true
  MapMode = 5
  Placement = pos=(56.6,-1.26e-14,1.26e-14) rot=(0.57735,0.57735,0.57735;2.0944rad)
  Support = -> [YZ_Plane005]
  sketch-geometry (4):
    g0: LineSegment StartX=-3.65 StartY=17.8 StartZ=0 EndX=-0.65 EndY=17.8 EndZ=0
    g1: LineSegment StartX=-0.65 StartY=17.8 StartZ=0 EndX=-0.65 EndY=14.2 EndZ=0
    g2: LineSegment StartX=-0.65 StartY=14.2 StartZ=0 EndX=-3.65 EndY=14.2 EndZ=0
    g3: LineSegment StartX=-3.65 StartY=14.2 StartZ=0 EndX=-3.65 EndY=17.8 EndZ=0
  constraints (12):
    c: Coincident(g0,g1)
    c: Coincident(g1,g2)
    c: Coincident(g2,g3)
    c: Coincident(g3,g0)
    c: Horizontal(g2)
    c: Vertical(g3)
    c: DistanceY(g3,g3) = 3.6
    c: DistanceX(g0,g0) = 3
    c: Horizontal(g0)
    c: Vertical(g1)
    c: DistanceX(g0,g-3) = 0.85
    c: PointOnObject(g0,g-5)
FEATURE [PartDesign::Pad] Pad020
  Direction = (1,1,1)
  Length = 3
  Length2 = 100
  Placement = pos=(0,0,0) rot=(0.57735,0.57735,0.57735;2.0944rad)
  Profile = -> Sketch047
  Type = 0
FEATURE [Sketcher::SketchObject] Sketch048
  ExternalGeometry = -> [Pad020]
  FullyConstrained = true
  MapMode = 5
  Placement = pos=(56.6,-6.68e-14,5.6e-14) rot=(-0.57735,-0.57735,0.57735;2.0944rad)
  Support = -> [Pad020]
  sketch-geometry (4):
    g0: LineSegment StartX=-6.25 StartY=-10.2 StartZ=0 EndX=1.95 EndY=-10.2 EndZ=0
    g1: LineSegment StartX=1.95 StartY=-10.2 StartZ=0 EndX=1.95 EndY=-17.8 EndZ=0
    g2: LineSegment StartX=1.95 StartY=-17.8 StartZ=0 EndX=-6.25 EndY=-17.8 EndZ=0
    g3: LineSegment StartX=-6.25 StartY=-17.8 StartZ=0 EndX=-6.25 EndY=-10.2 EndZ=0
  constraints (12):
    c: Coincident(g0,g1)
    c: Coincident(g1,g2)
    c: Coincident(g2,g3)
    c: Coincident(g3,g0)
    c: Horizontal(g0)
    c: Horizontal(g2)
    c: Vertical(g1)
    c: Vertical(g3)
    c: DistanceX(g0,g-3) = 2.6
    c: DistanceX(g-3,g0) = 2.6
    c: DistanceY(g3,g3) = 7.6
    c: Horizontal(g-4,g1)
FEATURE [PartDesign::Pad] Pad021
  BaseFeature = -> Pad020
  Direction = (1,1,1)
  Length = 1
  Length2 = 100
  Placement = pos=(0,0,0) rot=(0.57735,0.57735,0.57735;2.0944rad)
  Profile = -> Sketch048
  Type = 0
FEATURE [Sketcher::SketchObject] Sketch053
  ExternalGeometry = -> [Pad021]
  FullyConstrained = true
  MapMode = 5
  Placement = pos=(-2.08e-14,6.9e-15,17.8) rot=(0,0,-1;1.5708rad)
  Support = -> [Pad021]
  sketch-geometry (4):
    g0: LineSegment StartX=1.3 StartY=55.6 StartZ=0 EndX=2.9 EndY=55.6 EndZ=0
    g1: LineSegment StartX=2.9 StartY=55.6 StartZ=0 EndX=2.9 EndY=56.6 EndZ=0
    g2: LineSegment StartX=2.9 StartY=56.6 StartZ=0 EndX=1.3 EndY=56.6 EndZ=0
    g3: LineSegment StartX=1.3 StartY=56.6 StartZ=0 EndX=1.3 EndY=55.6 EndZ=0
  constraints (13):
    c: Coincident(g0,g1)
    c: Coincident(g1,g2)
    c: Coincident(g2,g3)
    c: Coincident(g3,g0)
    c: Horizontal(g0)
    c: Horizontal(g2)
    c: Vertical(g1)
    c: Vertical(g3)
    c: PointOnObject(g0,g-3)
    c: DistanceX(g2,g2) = 1.6
    c: DistanceY(g1,g1) = 1
    c: DistanceX(g-3,g-3) = 8.2
    c: DistanceX(g-3,g0) = 3.25
FEATURE [PartDesign::Pocket] Pocket018
  BaseFeature = -> Pad021
  Length = 3
  Length2 = 100
  Placement = pos=(0,0,0) rot=(0.57735,0.57735,0.57735;2.0944rad)
  Profile = -> Sketch053
  Type = 0
FEATURE [PartDesign::Body] Body005  label="Button-Power"
  Group = -> [ShapeBinder009,Sketch047,Pad020,Sketch048,Pad021,Sketch053,Pocket018]
  Origin = -> Origin005
  Tip = -> Pocket018
FEATURE [Sketcher::SketchObject] Sketch054
  FullyConstrained = true
  MapMode = 5
  Support = -> [XY_Plane007]
  sketch-geometry (4):
    g0: LineSegment StartX=0 StartY=6 StartZ=0 EndX=1 EndY=6 EndZ=0
    g1: LineSegment StartX=1 StartY=6 StartZ=0 EndX=1 EndY=-6 EndZ=0
    g2: LineSegment StartX=1 StartY=-6 StartZ=0 EndX=0 EndY=-6 EndZ=0
    g3: LineSegment StartX=0 StartY=-6 StartZ=0 EndX=0 EndY=6 EndZ=0
  constraints (11):
    c: Coincident(g0,g1)
    c: Coincident(g1,g2)
    c: Coincident(g2,g3)
    c: Coincident(g3,g0)
    c: Horizontal(g0)
    c: Horizontal(g2)
    c: Vertical(g3)
    c: PointOnObject(g0,g-2)
    c: Symmetric(g0,g1,g-1)
    c: DistanceX(g0,g0) = 1
    c: DistanceY(g1,g1) = 12
FEATURE [PartDesign::Pad] Pad024
  Direction = (1,1,1)
  Length = 1.6
  Length2 = 100
  Profile = -> Sketch054
  Type = 0
FEATURE [Sketcher::SketchObject] Sketch055
  ExternalGeometry = -> [Pad024]
  FullyConstrained = true
  MapMode = 5
  Placement = pos=(0,0,1.6) rot=(0,0,1;0rad)
  Support = -> [Pad024]
  sketch-geometry (4):
    g0: LineSegment StartX=-2.2 StartY=6 StartZ=0 EndX=1 EndY=6 EndZ=0
    g1: LineSegment StartX=1 StartY=6 StartZ=0 EndX=1 EndY=-6 EndZ=0
    g2: LineSegment StartX=1 StartY=-6 StartZ=0 EndX=-2.2 EndY=-6 EndZ=0
    g3: LineSegment StartX=-2.2 StartY=-6 StartZ=0 EndX=-2.2 EndY=6 EndZ=0
  constraints (10):
    c: Coincident(g0,g1)
    c: Coincident(g1,g2)
    c: Coincident(g2,g3)
    c: Coincident(g3,g0)
    c: Horizontal(g0)
    c: Horizontal(g2)
    c: DistanceX(g0,g0) = 3.2
    c: Vertical(g3)
    c: Coincident(g0,g-4)
    c: Coincident(g1,g-4)
FEATURE [PartDesign::Pad] Pad025
  BaseFeature = -> Pad024
  Direction = (1,1,1)
  Length = 2
  Length2 = 100
  Profile = -> Sketch055
  Type = 0
FEATURE [PartDesign::Body] Body007  label="Spacer"
  Group = -> [Sketch054,Pad024,Sketch055,Pad025]
  Origin = -> Origin007
  Placement = pos=(55,-41,8.5) rot=(0,0,1;0rad)
  Tip = -> Pad025
FEATURE [Mesh::Feature] Mesh  label="Spacer (Meshed)"
FEATURE [Mesh::Feature] Mesh001  label="Button-Power (Meshed)"
FEATURE [Mesh::Feature] Mesh002  label="Button-Reset (Meshed)"
FEATURE [Sketcher::SketchObject] Sketch056
  ExternalGeometry = -> [Pocket015]
  FullyConstrained = true
  MapMode = 5
  Placement = pos=(0,0,8.5) rot=(0,0,1;0rad)
  Support = -> [Pocket015]
  sketch-geometry (8):
    g0: LineSegment StartX=56.2 StartY=23.7 StartZ=0 EndX=55.2 EndY=23.7 EndZ=0
    g1: LineSegment StartX=55.2 StartY=23.7 StartZ=0 EndX=55.2 EndY=-23.7 EndZ=0
    g2: LineSegment StartX=55.2 StartY=-23.7 StartZ=0 EndX=56.2 EndY=-23.7 EndZ=0
    g3: LineSegment StartX=56.2 StartY=-23.7 StartZ=0 EndX=56.2 EndY=23.7 EndZ=0
    g4: LineSegment StartX=56.2 StartY=-31.7 StartZ=0 EndX=55.2 EndY=-31.7 EndZ=0
    g5: LineSegment StartX=55.2 StartY=-31.7 StartZ=0 EndX=55.2 EndY=-47.7 EndZ=0
    g6: LineSegment StartX=55.2 StartY=-47.7 StartZ=0 EndX=56.2 EndY=-47.7 EndZ=0
    g7: LineSegment StartX=56.2 StartY=-47.7 StartZ=0 EndX=56.2 EndY=-31.7 EndZ=0
  constraints (20):
    c: Coincident(g0,g1)
    c: Coincident(g1,g2)
    c: Coincident(g2,g3)
    c: Coincident(g3,g0)
    c: Horizontal(g0)
    c: Horizontal(g2)
    c: Coincident(g0,g-3)
    c: Coincident(g4,g5)
    c: Coincident(g5,g6)
    c: Coincident(g6,g7)
    c: Coincident(g7,g4)
    c: Horizontal(g4)
    c: Horizontal(g6)
    c: Vertical(g5)
    c: Coincident(g4,g-4)
    c: Coincident(g6,g-4)
    c: Coincident(g2,g-3)
    c: Vertical(g1)
    c: Equal(g4,g2)
    c: DistanceX(g6,g6) = 1
FEATURE [PartDesign::Pad] Pad026
  BaseFeature = -> Pocket015
  Direction = (1,1,1)
  Length = 1.5
  Length2 = 100
  Profile = -> Sketch056
  Type = 0
FEATURE [Sketcher::SketchObject] Sketch057
  ExternalGeometry = -> [Pad026]
  FullyConstrained = true
  MapMode = 5
  Placement = pos=(0,0,17.8) rot=(0,0,1;0rad)
  Support = -> [Pad026]
  sketch-geometry (4):
    g0: LineSegment StartX=56.2 StartY=-6.2 StartZ=0 EndX=56.8 EndY=-6.2 EndZ=0
    g1: LineSegment StartX=56.8 StartY=-6.2 StartZ=0 EndX=56.8 EndY=-6.5 EndZ=0
    g2: LineSegment StartX=56.8 StartY=-6.5 StartZ=0 EndX=56.2 EndY=-6.5 EndZ=0
    g3: LineSegment StartX=56.2 StartY=-6.5 StartZ=0 EndX=56.2 EndY=-6.2 EndZ=0
  constraints (10):
    c: Coincident(g0,g1)
    c: Coincident(g1,g2)
    c: Coincident(g2,g3)
    c: Coincident(g3,g0)
    c: Horizontal(g2)
    c: Vertical(g1)
    c: Vertical(g3)
    c: Coincident(g0,g-3)
    c: Coincident(g0,g-3)
    c: PointOnObject(g1,g-4)
FEATURE [PartDesign::Pocket] Pocket019
  BaseFeature = -> Pad026
  Length = 7.8
  Length2 = 100
  Profile = -> Sketch057
  Type = 0
FEATURE [Sketcher::SketchObject] Sketch058
  FullyConstrained = true
  MapMode = 5
  Placement = pos=(-58,0,0) rot=(0.57735,-0.57735,-0.57735;2.0944rad)
  Support = -> [Pocket019]
  sketch-geometry (8):
    g0: ArcOfCircle CenterX=-8 CenterY=12.6 CenterZ=0 NormalX=0 NormalY=0 NormalZ=1 AngleXU=0 Radius=0.6 StartAngle=1.5708 EndAngle=4.71239
    g1: ArcOfCircle CenterX=-2 CenterY=12.6 CenterZ=0 NormalX=0 NormalY=0 NormalZ=1 AngleXU=0 Radius=0.6 StartAngle=4.71239 EndAngle=7.85398
    g2: LineSegment StartX=-8 StartY=12 StartZ=0 EndX=-2 EndY=12 EndZ=0
    g3: LineSegment StartX=-8 StartY=13.2 StartZ=0 EndX=-2 EndY=13.2 EndZ=0
    g4: ArcOfCircle CenterX=2 CenterY=12.6 CenterZ=0 NormalX=0 NormalY=0 NormalZ=1 AngleXU=0 Radius=0.6 StartAngle=1.5708 EndAngle=4.71239
    g5: ArcOfCircle CenterX=8 CenterY=12.6 CenterZ=0 NormalX=0 NormalY=0 NormalZ=1 AngleXU=0 Radius=0.6 StartAngle=4.71239 EndAngle=7.85398
    g6: LineSegment StartX=2 StartY=12 StartZ=0 EndX=8 EndY=12 EndZ=0
    g7: LineSegment StartX=2 StartY=13.2 StartZ=0 EndX=8 EndY=13.2 EndZ=0
  constraints (20):
    c: Tangent(g0,g3) = 1.5708
    c: Tangent(g0,g2) = -1.5708
    c: Tangent(g2,g1) = -1.5708
    c: Tangent(g3,g1) = 1.5708
    c: Horizontal(g2)
    c: Equal(g0,g1)
    c: Tangent(g4,g7) = 1.5708
    c: Tangent(g4,g6) = -1.5708
    c: Tangent(g6,g5) = -1.5708
    c: Tangent(g7,g5) = 1.5708
    c: Horizontal(g6)
    c: Equal(g4,g5)
    c: Equal(g0,g4)
    c: Horizontal(g1,g4)
    c: Radius(g5) = 0.6
    c: Equal(g2,g6)
    c: DistanceX(g2,g2) = 6
    c: DistanceX(g-1,g4) = 2
    c: DistanceX(g1,g-1) = 2
    c: DistanceY(g-1,g0) = 12
FEATURE [PartDesign::Pocket] Pocket020
  BaseFeature = -> Pocket019
  Length = 2.8
  Length2 = 100
  Profile = -> Sketch058
  Type = 0
FEATURE [PartDesign::ShapeBinder] ShapeBinder010
  Support = -> [Sketch]
  TraceSupport = false
FEATURE [Sketcher::SketchObject] Sketch059
  ExternalGeometry = -> [ShapeBinder010,Pocket020]
  FullyConstrained = true
  MapMode = 5
  Placement = pos=(0,-50.5,0) rot=(1,0,0;1.5708rad)
  Support = -> [Pocket020]
  sketch-geometry (4):
    g0: LineSegment StartX=-25.4 StartY=17.8 StartZ=0 EndX=-12.4 EndY=17.8 EndZ=0
    g1: LineSegment StartX=-12.4 StartY=17.8 StartZ=0 EndX=-12.4 EndY=12.8 EndZ=0
    g2: LineSegment StartX=-12.4 StartY=12.8 StartZ=0 EndX=-25.4 EndY=12.8 EndZ=0
    g3: LineSegment StartX=-25.4 StartY=12.8 StartZ=0 EndX=-25.4 EndY=17.8 EndZ=0
  constraints (12):
    c: Coincident(g0,g1)
    c: Coincident(g1,g2)
    c: Coincident(g2,g3)
    c: Coincident(g3,g0)
    c: Horizontal(g0)
    c: Horizontal(g2)
    c: Vertical(g1)
    c: Vertical(g3)
    c: PointOnObject(g0,g-5)
    c: DistanceX(g2,g-3) = 2
    c: DistanceX(g-4,g1) = 2
    c: DistanceY(g1,g1) = 5
FEATURE [PartDesign::Pocket] Pocket021
  BaseFeature = -> Pocket020
  Length = 2.8
  Length2 = 100
  Profile = -> Sketch059
  Type = 0
FEATURE [PartDesign::Body] Body002  label="Bottom"
  Group = -> [ShapeBinder004,ShapeBinder005,ShapeBinder008,Sketch021,Pad012,Sketch025,Pocket003,Sketch026,Pad014,Sketch027,Pocket004,Sketch028,Pocket005,Sketch029,Pocket006,Sketch030,Pocket007,Sketch032,Pocket009,Sketch037,Pocket012,Sketch043,Pocket015,Sketch056,Pad026,Sketch057,Pocket019,Sketch058,Pocket020,ShapeBinder010,Sketch059,Pocket021]
  Origin = -> Origin002
  Tip = -> Pocket021
FEATURE [PartDesign::Chamfer] Chamfer001
  Angle = 45
  Base = -> Pocket016 [Edge42,Edge43,Edge44,Edge45]
  BaseFeature = -> Pocket016
  ChamferType = 0
  FlipDirection = false
  Size = 1.4
  Size2 = 1
  SupportTransform = false
FEATURE [PartDesign::Body] Body003  label="Cover"
  Group = -> [ShapeBinder006,ShapeBinder007,Sketch022,Pad013,Sketch023,Pocket001,Sketch024,Pocket002,Sketch031,Pocket008,Sketch038,Pad017,Sketch044,Pad018,Sketch045,Pad019,Sketch046,Pocket016,Chamfer001]
  Origin = -> Origin003
  Tip = -> Chamfer001
